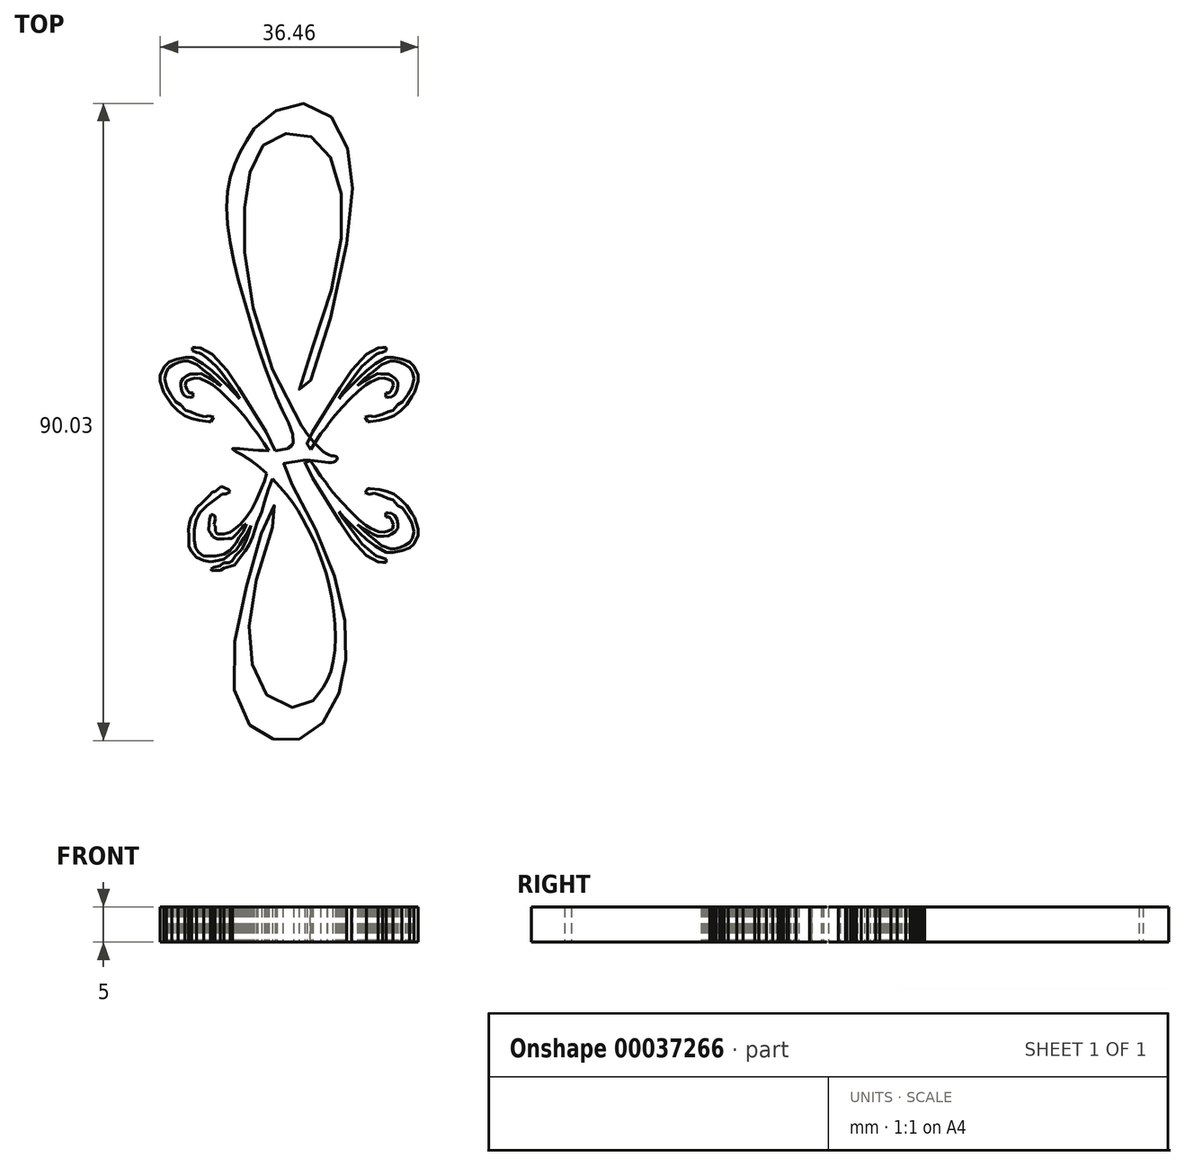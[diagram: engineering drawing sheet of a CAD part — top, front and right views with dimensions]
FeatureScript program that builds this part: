
annotation { "Feature Type Name" : "Feature", "Feature Type Description" : "" }
export const myFeature = defineFeature(function(context is Context, id is Id, definition is map)
    precondition{}
    {
        {
            var Q0;
            Q0=qCreatedBy(makeId("Top.planeOp"),FACE);
            var sketch = newSketch(context, id + "F0", { "sketchPlane" : qUnion([Q0])});
            skFitSpline(sketch, "E0", {"points": [v(-4.98, 52.48) * mm, v(-8.77, 43.42) * mm, v(-5.8, 26.25) * mm, v(-0.94, 12.64) * mm, v(0, 7.4) * mm, v(-8, 7.3) * mm, v(-6.47, 6.29) * mm, v(-0.6, 1.07) * mm, v(2.95, -4.65) * mm, v(5.7, -12.25) * mm, v(6.06, -23.55) * mm, v(3.37, -28.3) * mm], "startDerivative": vector(-52, -82.41) * mm, "endDerivative": vector(-44.36, -53.84) * mm});
            skFitSpline(sketch, "E1", {"points": [v(3.37, -28.3) * mm, v(0.95, -29.26) * mm, v(-3.07, -27.64) * mm, v(-5.46, -21.7) * mm, v(-4.69, -11.43) * mm, v(-1.8, -0.83) * mm, v(-2.3, -0.83) * mm, v(-5.52, -10.23) * mm, v(-7.9, -25.88) * mm, v(-4.68, -32.69) * mm, v(-1.17, -33.88) * mm, v(2.55, -33.39) * mm, v(6.27, -28.97) * mm, v(7.96, -23) * mm, v(7.32, -14.02) * mm, v(2.27, -1.25) * mm, v(-0.89, 5.13) * mm, v(-0.46, 5.24) * mm, v(2.3, 5.67) * mm, v(6.42, 5.45) * mm, v(6.75, 6.1) * mm, v(5.51, 6.44) * mm, v(-1.92, 17.38) * mm, v(-6.32, 34.87) * mm, v(-6.05, 43.62) * mm, v(-4.64, 48.73) * mm, v(-2.14, 51.4) * mm, v(1.12, 51.83) * mm, v(3.95, 50.9) * mm, v(6.55, 46.66) * mm, v(7.48, 38.19) * mm, v(4.22, 24.27) * mm, v(1.45, 15.15) * mm, v(2.32, 15.69) * mm, v(8.13, 36.5) * mm, v(8.57, 48.24) * mm, v(6.07, 54) * mm, v(1.88, 56.06) * mm, v(-1.87, 55.03) * mm, v(-4.98, 52.48) * mm], "startDerivative": vector(-130.49, -80) * mm, "endDerivative": vector(-141.72, -134) * mm});
            skLineSegment(sketch, "E2", {"start": v(-2.02, 7) * mm, "end": v(-3.27, 9.64) * mm});
            skLineSegment(sketch, "E3", {"start": v(-3.27, 9.64) * mm, "end": v(-7.15, 15.86) * mm});
            skLineSegment(sketch, "E4", {"start": v(-7.15, 15.86) * mm, "end": v(-8.78, 18.34) * mm});
            skLineSegment(sketch, "E5", {"start": v(-8.78, 18.34) * mm, "end": v(-10.9, 20.62) * mm});
            skLineSegment(sketch, "E6", {"start": v(-10.9, 20.62) * mm, "end": v(-12.53, 21.5) * mm});
            skLineSegment(sketch, "E7", {"start": v(-12.53, 21.5) * mm, "end": v(-13.21, 21.57) * mm});
            skLineSegment(sketch, "E8", {"start": v(-13.21, 21.57) * mm, "end": v(-13.68, 21.57) * mm});
            skLineSegment(sketch, "E9", {"start": v(-13.68, 21.57) * mm, "end": v(-13.68, 21.12) * mm});
            skLineSegment(sketch, "E10", {"start": v(-13.68, 21.12) * mm, "end": v(-13.13, 20.91) * mm});
            skLineSegment(sketch, "E11", {"start": v(-13.13, 20.91) * mm, "end": v(-12.73, 20.8) * mm});
            skLineSegment(sketch, "E12", {"start": v(-12.73, 20.8) * mm, "end": v(-12.31, 20.64) * mm});
            skLineSegment(sketch, "E13", {"start": v(-12.31, 20.64) * mm, "end": v(-11.6, 20.07) * mm});
            skLineSegment(sketch, "E14", {"start": v(-11.6, 20.07) * mm, "end": v(-10.29, 18.92) * mm});
            skLineSegment(sketch, "E15", {"start": v(-10.29, 18.92) * mm, "end": v(-9.6, 18.08) * mm});
            skLineSegment(sketch, "E16", {"start": v(-9.6, 18.08) * mm, "end": v(-7.57, 15.33) * mm});
            skLineSegment(sketch, "E17", {"start": v(-7.57, 15.33) * mm, "end": v(-7.02, 14.38) * mm});
            skLineSegment(sketch, "E18", {"start": v(-7.02, 14.38) * mm, "end": v(-7.75, 15.19) * mm});
            skLineSegment(sketch, "E19", {"start": v(-7.75, 15.19) * mm, "end": v(-8.94, 16.4) * mm});
            skLineSegment(sketch, "E20", {"start": v(-8.94, 16.4) * mm, "end": v(-9.87, 17.33) * mm});
            skLineSegment(sketch, "E21", {"start": v(-9.87, 17.33) * mm, "end": v(-10.96, 18.37) * mm});
            skLineSegment(sketch, "E22", {"start": v(-10.96, 18.37) * mm, "end": v(-12.2, 19.27) * mm});
            skLineSegment(sketch, "E23", {"start": v(-12.2, 19.27) * mm, "end": v(-13.69, 20.18) * mm});
            skLineSegment(sketch, "E24", {"start": v(-13.69, 20.18) * mm, "end": v(-14.65, 20.18) * mm});
            skLineSegment(sketch, "E25", {"start": v(-14.65, 20.18) * mm, "end": v(-15.93, 19.93) * mm});
            skLineSegment(sketch, "E26", {"start": v(-15.93, 19.93) * mm, "end": v(-16.96, 19.55) * mm});
            skLineSegment(sketch, "E27", {"start": v(-16.96, 19.55) * mm, "end": v(-17.62, 18.92) * mm});
            skLineSegment(sketch, "E28", {"start": v(-17.62, 18.92) * mm, "end": v(-18.23, 17.73) * mm});
            skLineSegment(sketch, "E29", {"start": v(-18.23, 17.73) * mm, "end": v(-18.23, 16.85) * mm});
            skLineSegment(sketch, "E30", {"start": v(-18.23, 16.85) * mm, "end": v(-17.72, 15.2) * mm});
            skLineSegment(sketch, "E31", {"start": v(-17.72, 15.2) * mm, "end": v(-17.34, 14.65) * mm});
            skLineSegment(sketch, "E32", {"start": v(-17.34, 14.65) * mm, "end": v(-16.6, 13.55) * mm});
            skLineSegment(sketch, "E33", {"start": v(-16.6, 13.55) * mm, "end": v(-15.74, 12.65) * mm});
            skLineSegment(sketch, "E34", {"start": v(-15.74, 12.65) * mm, "end": v(-14.75, 11.92) * mm});
            skLineSegment(sketch, "E35", {"start": v(-14.75, 11.92) * mm, "end": v(-13.78, 11.54) * mm});
            skLineSegment(sketch, "E36", {"start": v(-13.78, 11.54) * mm, "end": v(-12.74, 11.27) * mm});
            skLineSegment(sketch, "E37", {"start": v(-12.74, 11.27) * mm, "end": v(-11.4, 11.13) * mm});
            skLineSegment(sketch, "E38", {"start": v(-11.4, 11.13) * mm, "end": v(-11.1, 11.13) * mm});
            skLineSegment(sketch, "E39", {"start": v(-11.1, 11.13) * mm, "end": v(-10.69, 11.72) * mm});
            skLineSegment(sketch, "E40", {"start": v(-10.69, 11.72) * mm, "end": v(-11.34, 11.93) * mm});
            skLineSegment(sketch, "E41", {"start": v(-11.34, 11.93) * mm, "end": v(-11.97, 11.79) * mm});
            skLineSegment(sketch, "E42", {"start": v(-11.97, 11.79) * mm, "end": v(-13.1, 12.13) * mm});
            skLineSegment(sketch, "E43", {"start": v(-13.1, 12.13) * mm, "end": v(-13.94, 12.52) * mm});
            skLineSegment(sketch, "E44", {"start": v(-13.94, 12.52) * mm, "end": v(-14.63, 12.7) * mm});
            skLineSegment(sketch, "E45", {"start": v(-14.63, 12.7) * mm, "end": v(-15.38, 13.52) * mm});
            skLineSegment(sketch, "E46", {"start": v(-15.38, 13.52) * mm, "end": v(-16, 13.89) * mm});
            skLineSegment(sketch, "E47", {"start": v(-16, 13.89) * mm, "end": v(-16.73, 14.92) * mm});
            skLineSegment(sketch, "E48", {"start": v(-16.73, 14.92) * mm, "end": v(-17.32, 15.96) * mm});
            skLineSegment(sketch, "E49", {"start": v(-17.32, 15.96) * mm, "end": v(-17.61, 17.2) * mm});
            skLineSegment(sketch, "E50", {"start": v(-17.61, 17.2) * mm, "end": v(-17.39, 18.18) * mm});
            skLineSegment(sketch, "E51", {"start": v(-17.39, 18.18) * mm, "end": v(-17.01, 18.74) * mm});
            skLineSegment(sketch, "E52", {"start": v(-17.01, 18.74) * mm, "end": v(-16.37, 19.15) * mm});
            skLineSegment(sketch, "E53", {"start": v(-16.37, 19.15) * mm, "end": v(-15.65, 19.46) * mm});
            skLineSegment(sketch, "E54", {"start": v(-15.65, 19.46) * mm, "end": v(-14.9, 19.65) * mm});
            skLineSegment(sketch, "E55", {"start": v(-14.9, 19.65) * mm, "end": v(-14.33, 19.65) * mm});
            skLineSegment(sketch, "E56", {"start": v(-14.33, 19.65) * mm, "end": v(-13.07, 19.2) * mm});
            skLineSegment(sketch, "E57", {"start": v(-13.07, 19.2) * mm, "end": v(-11.84, 18.16) * mm});
            skLineSegment(sketch, "E58", {"start": v(-11.84, 18.16) * mm, "end": v(-11.22, 17.7) * mm});
            skLineSegment(sketch, "E59", {"start": v(-11.22, 17.7) * mm, "end": v(-10.54, 17.07) * mm});
            skLineSegment(sketch, "E60", {"start": v(-10.54, 17.07) * mm, "end": v(-10.05, 16.63) * mm});
            skLineSegment(sketch, "E61", {"start": v(-10.05, 16.63) * mm, "end": v(-9.63, 16.2) * mm});
            skLineSegment(sketch, "E62", {"start": v(-9.63, 16.2) * mm, "end": v(-10.22, 16.58) * mm});
            skLineSegment(sketch, "E63", {"start": v(-10.22, 16.58) * mm, "end": v(-10.56, 16.83) * mm});
            skLineSegment(sketch, "E64", {"start": v(-10.56, 16.83) * mm, "end": v(-11.37, 17.3) * mm});
            skLineSegment(sketch, "E65", {"start": v(-11.37, 17.3) * mm, "end": v(-11.78, 17.53) * mm});
            skLineSegment(sketch, "E66", {"start": v(-11.78, 17.53) * mm, "end": v(-12.48, 17.88) * mm});
            skLineSegment(sketch, "E67", {"start": v(-12.48, 17.88) * mm, "end": v(-12.9, 17.84) * mm});
            skLineSegment(sketch, "E68", {"start": v(-12.9, 17.84) * mm, "end": v(-13.36, 17.87) * mm});
            skLineSegment(sketch, "E69", {"start": v(-13.36, 17.87) * mm, "end": v(-14, 17.81) * mm});
            skLineSegment(sketch, "E70", {"start": v(-14, 17.81) * mm, "end": v(-14.47, 17.56) * mm});
            skLineSegment(sketch, "E71", {"start": v(-14.47, 17.56) * mm, "end": v(-15, 17.2) * mm});
            skLineSegment(sketch, "E72", {"start": v(-15, 17.2) * mm, "end": v(-15.35, 16.72) * mm});
            skLineSegment(sketch, "E73", {"start": v(-15.35, 16.72) * mm, "end": v(-15.35, 16.18) * mm});
            skLineSegment(sketch, "E74", {"start": v(-15.35, 16.18) * mm, "end": v(-15.22, 15.48) * mm});
            skLineSegment(sketch, "E75", {"start": v(-15.22, 15.48) * mm, "end": v(-14.93, 14.95) * mm});
            skLineSegment(sketch, "E76", {"start": v(-14.93, 14.95) * mm, "end": v(-14.48, 14.6) * mm});
            skLineSegment(sketch, "E77", {"start": v(-14.48, 14.6) * mm, "end": v(-13.93, 14.54) * mm});
            skLineSegment(sketch, "E78", {"start": v(-13.93, 14.54) * mm, "end": v(-13.63, 14.57) * mm});
            skLineSegment(sketch, "E79", {"start": v(-13.63, 14.57) * mm, "end": v(-13.63, 15.16) * mm});
            skLineSegment(sketch, "E80", {"start": v(-13.63, 15.16) * mm, "end": v(-14.12, 15.17) * mm});
            skLineSegment(sketch, "E81", {"start": v(-14.12, 15.17) * mm, "end": v(-14.46, 15.6) * mm});
            skLineSegment(sketch, "E82", {"start": v(-14.46, 15.6) * mm, "end": v(-14.7, 16.22) * mm});
            skLineSegment(sketch, "E83", {"start": v(-14.7, 16.22) * mm, "end": v(-14.58, 16.85) * mm});
            skLineSegment(sketch, "E84", {"start": v(-14.58, 16.85) * mm, "end": v(-14.02, 17.1) * mm});
            skLineSegment(sketch, "E85", {"start": v(-14.02, 17.1) * mm, "end": v(-13.36, 17.27) * mm});
            skLineSegment(sketch, "E86", {"start": v(-13.36, 17.27) * mm, "end": v(-12.62, 17.2) * mm});
            skLineSegment(sketch, "E87", {"start": v(-12.62, 17.2) * mm, "end": v(-11.5, 16.7) * mm});
            skLineSegment(sketch, "E88", {"start": v(-11.5, 16.7) * mm, "end": v(-10.84, 16.32) * mm});
            skLineSegment(sketch, "E89", {"start": v(-10.84, 16.32) * mm, "end": v(-9.74, 15.45) * mm});
            skLineSegment(sketch, "E90", {"start": v(-9.74, 15.45) * mm, "end": v(-8.7, 14.39) * mm});
            skLineSegment(sketch, "E91", {"start": v(-8.7, 14.39) * mm, "end": v(-7.42, 13.06) * mm});
            skLineSegment(sketch, "E92", {"start": v(-7.42, 13.06) * mm, "end": v(-6.14, 11.64) * mm});
            skLineSegment(sketch, "E93", {"start": v(-6.14, 11.64) * mm, "end": v(-5.4, 10.6) * mm});
            skLineSegment(sketch, "E94", {"start": v(-5.4, 10.6) * mm, "end": v(-5.29, 10.43) * mm});
            skLineSegment(sketch, "E95", {"start": v(-5.29, 10.43) * mm, "end": v(-4.44, 9.38) * mm});
            skLineSegment(sketch, "E96", {"start": v(-4.44, 9.38) * mm, "end": v(-3.6, 8.08) * mm});
            skLineSegment(sketch, "E97", {"start": v(-3.6, 8.08) * mm, "end": v(-2.89, 6.99) * mm});
            skLineSegment(sketch, "E98", {"start": v(-3.23, 3.82) * mm, "end": v(-3.53, 2.65) * mm});
            skLineSegment(sketch, "E99", {"start": v(-3.53, 2.65) * mm, "end": v(-4.67, 0) * mm});
            skLineSegment(sketch, "E100", {"start": v(-4.67, 0) * mm, "end": v(-5.32, -1.28) * mm});
            skLineSegment(sketch, "E101", {"start": v(-5.32, -1.28) * mm, "end": v(-5.98, -2.28) * mm});
            skLineSegment(sketch, "E102", {"start": v(-5.98, -2.28) * mm, "end": v(-6.87, -3.36) * mm});
            skLineSegment(sketch, "E103", {"start": v(-6.87, -3.36) * mm, "end": v(-7.87, -4.23) * mm});
            skLineSegment(sketch, "E104", {"start": v(-7.87, -4.23) * mm, "end": v(-8.32, -4.54) * mm});
            skLineSegment(sketch, "E105", {"start": v(-8.32, -4.54) * mm, "end": v(-9.22, -4.74) * mm});
            skLineSegment(sketch, "E106", {"start": v(-9.22, -4.74) * mm, "end": v(-10.16, -4.74) * mm});
            skLineSegment(sketch, "E107", {"start": v(-10.16, -4.74) * mm, "end": v(-10.42, -4.36) * mm});
            skLineSegment(sketch, "E108", {"start": v(-10.42, -4.36) * mm, "end": v(-10.42, -3.71) * mm});
            skLineSegment(sketch, "E109", {"start": v(-10.42, -3.71) * mm, "end": v(-10.63, -3.43) * mm});
            skLineSegment(sketch, "E110", {"start": v(-10.63, -3.43) * mm, "end": v(-10.45, -2.6) * mm});
            skLineSegment(sketch, "E111", {"start": v(-10.45, -2.6) * mm, "end": v(-10.54, -2.17) * mm});
            skLineSegment(sketch, "E112", {"start": v(-10.54, -2.17) * mm, "end": v(-10.74, -2.06) * mm});
            skLineSegment(sketch, "E113", {"start": v(-10.74, -2.06) * mm, "end": v(-11.05, -2.06) * mm});
            skLineSegment(sketch, "E114", {"start": v(-11.05, -2.06) * mm, "end": v(-11.3, -2.67) * mm});
            skLineSegment(sketch, "E115", {"start": v(-11.3, -2.67) * mm, "end": v(-11.31, -3.32) * mm});
            skLineSegment(sketch, "E116", {"start": v(-11.31, -3.32) * mm, "end": v(-11.38, -4.27) * mm});
            skLineSegment(sketch, "E117", {"start": v(-11.38, -4.27) * mm, "end": v(-11.1, -4.7) * mm});
            skLineSegment(sketch, "E118", {"start": v(-11.1, -4.7) * mm, "end": v(-10.84, -5.13) * mm});
            skLineSegment(sketch, "E119", {"start": v(-10.84, -5.13) * mm, "end": v(-10.2, -5.45) * mm});
            skLineSegment(sketch, "E120", {"start": v(-10.2, -5.45) * mm, "end": v(-9.22, -5.45) * mm});
            skLineSegment(sketch, "E121", {"start": v(-9.22, -5.45) * mm, "end": v(-8.63, -5.4) * mm});
            skLineSegment(sketch, "E122", {"start": v(-8.63, -5.4) * mm, "end": v(-8.1, -5.4) * mm});
            skLineSegment(sketch, "E123", {"start": v(-8.1, -5.4) * mm, "end": v(-7.24, -4.56) * mm});
            skLineSegment(sketch, "E124", {"start": v(-7.24, -4.56) * mm, "end": v(-6.54, -3.72) * mm});
            skLineSegment(sketch, "E125", {"start": v(-6.54, -3.72) * mm, "end": v(-6.03, -3.34) * mm});
            skLineSegment(sketch, "E126", {"start": v(-6.03, -3.34) * mm, "end": v(-6.5, -4.46) * mm});
            skLineSegment(sketch, "E127", {"start": v(-6.5, -4.46) * mm, "end": v(-7.07, -5.24) * mm});
            skLineSegment(sketch, "E128", {"start": v(-7.07, -5.24) * mm, "end": v(-7.52, -6.04) * mm});
            skLineSegment(sketch, "E129", {"start": v(-7.52, -6.04) * mm, "end": v(-8.32, -7.05) * mm});
            skLineSegment(sketch, "E130", {"start": v(-8.32, -7.05) * mm, "end": v(-9.24, -7.65) * mm});
            skLineSegment(sketch, "E131", {"start": v(-9.24, -7.65) * mm, "end": v(-10.41, -7.9) * mm});
            skLineSegment(sketch, "E132", {"start": v(-10.41, -7.9) * mm, "end": v(-11.4, -7.9) * mm});
            skLineSegment(sketch, "E133", {"start": v(-11.4, -7.9) * mm, "end": v(-12.18, -7.9) * mm});
            skLineSegment(sketch, "E134", {"start": v(-12.18, -7.9) * mm, "end": v(-12.86, -7.3) * mm});
            skLineSegment(sketch, "E135", {"start": v(-12.86, -7.3) * mm, "end": v(-13.25, -6.73) * mm});
            skLineSegment(sketch, "E136", {"start": v(-13.25, -6.73) * mm, "end": v(-13.4, -5.68) * mm});
            skLineSegment(sketch, "E137", {"start": v(-13.4, -5.68) * mm, "end": v(-13.43, -4.14) * mm});
            skLineSegment(sketch, "E138", {"start": v(-13.43, -4.14) * mm, "end": v(-13.19, -2.86) * mm});
            skLineSegment(sketch, "E139", {"start": v(-13.19, -2.86) * mm, "end": v(-12.68, -1.8) * mm});
            skLineSegment(sketch, "E140", {"start": v(-12.68, -1.8) * mm, "end": v(-11.68, -0.78) * mm});
            skLineSegment(sketch, "E141", {"start": v(-11.68, -0.78) * mm, "end": v(-10.65, 0) * mm});
            skLineSegment(sketch, "E142", {"start": v(-10.65, 0) * mm, "end": v(-9.85, 0.55) * mm});
            skLineSegment(sketch, "E143", {"start": v(-9.85, 0.55) * mm, "end": v(-9.48, 0.86) * mm});
            skLineSegment(sketch, "E144", {"start": v(-9.48, 0.86) * mm, "end": v(-8.95, 0.86) * mm});
            skLineSegment(sketch, "E145", {"start": v(-8.95, 0.86) * mm, "end": v(-8.37, 1.21) * mm});
            skLineSegment(sketch, "E146", {"start": v(-8.37, 1.21) * mm, "end": v(-8.58, 1.52) * mm});
            skLineSegment(sketch, "E147", {"start": v(-8.58, 1.52) * mm, "end": v(-9.6, 1.97) * mm});
            skLineSegment(sketch, "E148", {"start": v(-9.6, 1.97) * mm, "end": v(-10.5, 1.2) * mm});
            skLineSegment(sketch, "E149", {"start": v(-10.5, 1.2) * mm, "end": v(-10.84, 1.2) * mm});
            skLineSegment(sketch, "E150", {"start": v(-10.84, 1.2) * mm, "end": v(-11.37, 0.56) * mm});
            skLineSegment(sketch, "E151", {"start": v(-11.37, 0.56) * mm, "end": v(-12.27, -0.35) * mm});
            skLineSegment(sketch, "E152", {"start": v(-12.27, -0.35) * mm, "end": v(-13.01, -1.03) * mm});
            skLineSegment(sketch, "E153", {"start": v(-13.01, -1.03) * mm, "end": v(-13.62, -2.1) * mm});
            skLineSegment(sketch, "E154", {"start": v(-13.62, -2.1) * mm, "end": v(-13.85, -2.41) * mm});
            skLineSegment(sketch, "E155", {"start": v(-13.85, -2.41) * mm, "end": v(-14.03, -3.05) * mm});
            skLineSegment(sketch, "E156", {"start": v(-14.03, -3.05) * mm, "end": v(-14.23, -4.16) * mm});
            skLineSegment(sketch, "E157", {"start": v(-14.23, -4.16) * mm, "end": v(-14.2, -5.04) * mm});
            skLineSegment(sketch, "E158", {"start": v(-14.2, -5.04) * mm, "end": v(-14.2, -6.57) * mm});
            skLineSegment(sketch, "E159", {"start": v(-14.2, -6.57) * mm, "end": v(-13.8, -7.26) * mm});
            skLineSegment(sketch, "E160", {"start": v(-13.8, -7.26) * mm, "end": v(-13.1, -8.04) * mm});
            skLineSegment(sketch, "E161", {"start": v(-13.1, -8.04) * mm, "end": v(-12.11, -8.5) * mm});
            skLineSegment(sketch, "E162", {"start": v(-12.11, -8.5) * mm, "end": v(-11.1, -8.71) * mm});
            skLineSegment(sketch, "E163", {"start": v(-11.1, -8.71) * mm, "end": v(-10.08, -8.52) * mm});
            skLineSegment(sketch, "E164", {"start": v(-10.08, -8.52) * mm, "end": v(-9.26, -8.33) * mm});
            skLineSegment(sketch, "E165", {"start": v(-9.26, -8.33) * mm, "end": v(-8.46, -7.7) * mm});
            skLineSegment(sketch, "E166", {"start": v(-8.46, -7.7) * mm, "end": v(-7.54, -7.03) * mm});
            skLineSegment(sketch, "E167", {"start": v(-7.54, -7.03) * mm, "end": v(-7, -6.3) * mm});
            skLineSegment(sketch, "E168", {"start": v(-7, -6.3) * mm, "end": v(-6.41, -5.36) * mm});
            skLineSegment(sketch, "E169", {"start": v(-6.41, -5.36) * mm, "end": v(-5.9, -4.6) * mm});
            skLineSegment(sketch, "E170", {"start": v(-5.9, -4.6) * mm, "end": v(-5.43, -3.59) * mm});
            skLineSegment(sketch, "E171", {"start": v(-5.43, -3.59) * mm, "end": v(-5.76, -4.64) * mm});
            skLineSegment(sketch, "E172", {"start": v(-5.76, -4.64) * mm, "end": v(-6.14, -5.8) * mm});
            skLineSegment(sketch, "E173", {"start": v(-6.14, -5.8) * mm, "end": v(-6.77, -6.99) * mm});
            skLineSegment(sketch, "E174", {"start": v(-6.77, -6.99) * mm, "end": v(-7.57, -7.8) * mm});
            skLineSegment(sketch, "E175", {"start": v(-7.57, -7.8) * mm, "end": v(-8.08, -8.55) * mm});
            skLineSegment(sketch, "E176", {"start": v(-8.08, -8.55) * mm, "end": v(-8.56, -8.84) * mm});
            skLineSegment(sketch, "E177", {"start": v(-8.56, -8.84) * mm, "end": v(-9.27, -8.85) * mm});
            skLineSegment(sketch, "E178", {"start": v(-9.27, -8.85) * mm, "end": v(-9.78, -9.25) * mm});
            skLineSegment(sketch, "E179", {"start": v(-9.78, -9.25) * mm, "end": v(-10.6, -9.5) * mm});
            skLineSegment(sketch, "E180", {"start": v(-10.6, -9.5) * mm, "end": v(-11.1, -9.74) * mm});
            skLineSegment(sketch, "E181", {"start": v(-11.1, -9.74) * mm, "end": v(-10.96, -10) * mm});
            skLineSegment(sketch, "E182", {"start": v(-10.96, -10) * mm, "end": v(-10.5, -9.91) * mm});
            skLineSegment(sketch, "E183", {"start": v(-10.5, -9.91) * mm, "end": v(-9.74, -9.91) * mm});
            skLineSegment(sketch, "E184", {"start": v(-9.74, -9.91) * mm, "end": v(-9.23, -9.6) * mm});
            skLineSegment(sketch, "E185", {"start": v(-9.23, -9.6) * mm, "end": v(-8.32, -9.37) * mm});
            skLineSegment(sketch, "E186", {"start": v(-8.32, -9.37) * mm, "end": v(-7.69, -9.14) * mm});
            skLineSegment(sketch, "E187", {"start": v(-7.69, -9.14) * mm, "end": v(-6.89, -8.03) * mm});
            skLineSegment(sketch, "E188", {"start": v(-6.89, -8.03) * mm, "end": v(-6.24, -7.18) * mm});
            skLineSegment(sketch, "E189", {"start": v(-6.24, -7.18) * mm, "end": v(-5.7, -6.27) * mm});
            skLineSegment(sketch, "E190", {"start": v(-5.7, -6.27) * mm, "end": v(-5.2, -5.16) * mm});
            skLineSegment(sketch, "E191", {"start": v(-5.2, -5.16) * mm, "end": v(-4.53, -3.14) * mm});
            skLineSegment(sketch, "E192", {"start": v(-4.53, -3.14) * mm, "end": v(-3.9, -1.64) * mm});
            skLineSegment(sketch, "E193", {"start": v(-3.9, -1.64) * mm, "end": v(-3.49, -0.28) * mm});
            skLineSegment(sketch, "E194", {"start": v(-3.49, -0.28) * mm, "end": v(-2.97, 1.56) * mm});
            skLineSegment(sketch, "E195", {"start": v(-2.97, 1.56) * mm, "end": v(-2.4, 3.03) * mm});
            skLineSegment(sketch, "E196", {"start": v(1.96, 5.66) * mm, "end": v(1.96, 4.6) * mm});
            skLineSegment(sketch, "E197", {"start": v(1.96, 4.6) * mm, "end": v(2.18, 3.77) * mm});
            skLineSegment(sketch, "E198", {"start": v(2.18, 3.77) * mm, "end": v(2.43, 2.6) * mm});
            skLineSegment(sketch, "E199", {"start": v(2.43, 2.6) * mm, "end": v(2.7, 1.46) * mm});
            skLineSegment(sketch, "E200", {"start": v(2.7, 1.46) * mm, "end": v(2.95, 0.59) * mm});
            skLineSegment(sketch, "E201", {"start": v(2.95, 0.59) * mm, "end": v(3.28, -0.15) * mm});
            skLineSegment(sketch, "E202", {"start": v(3.28, -0.15) * mm, "end": v(3.44, -1.19) * mm});
            skLineSegment(sketch, "E203", {"start": v(3.44, -1.19) * mm, "end": v(4.07, -2.5) * mm});
            skLineSegment(sketch, "E204", {"start": v(4.07, -2.5) * mm, "end": v(4.28, -3.22) * mm});
            skLineSegment(sketch, "E205", {"start": v(4.28, -3.22) * mm, "end": v(4.63, -3.77) * mm});
            skLineSegment(sketch, "E206", {"start": v(4.63, -3.77) * mm, "end": v(5.03, -4.34) * mm});
            skLineSegment(sketch, "E207", {"start": v(5.03, -4.34) * mm, "end": v(5.42, -4.97) * mm});
            skLineSegment(sketch, "E208", {"start": v(5.42, -4.97) * mm, "end": v(5.9, -5.47) * mm});
            skLineSegment(sketch, "E209", {"start": v(5.9, -5.47) * mm, "end": v(6.98, -6.44) * mm});
            skLineSegment(sketch, "E210", {"start": v(6.98, -6.44) * mm, "end": v(7.3, -6.55) * mm});
            skLineSegment(sketch, "E211", {"start": v(7.3, -6.55) * mm, "end": v(7.53, -6.73) * mm});
            skLineSegment(sketch, "E212", {"start": v(7.53, -6.73) * mm, "end": v(7.85, -6.8) * mm});
            skLineSegment(sketch, "E213", {"start": v(7.85, -6.8) * mm, "end": v(8.32, -6.66) * mm});
            skLineSegment(sketch, "E214", {"start": v(8.32, -6.66) * mm, "end": v(7.94, -6.02) * mm});
            skLineSegment(sketch, "E215", {"start": v(7.94, -6.02) * mm, "end": v(7.48, -5.93) * mm});
            skLineSegment(sketch, "E216", {"start": v(7.48, -5.93) * mm, "end": v(7.04, -5.33) * mm});
            skLineSegment(sketch, "E217", {"start": v(7.04, -5.33) * mm, "end": v(6.23, -4.45) * mm});
            skLineSegment(sketch, "E218", {"start": v(6.23, -4.45) * mm, "end": v(5.6, -3.74) * mm});
            skLineSegment(sketch, "E219", {"start": v(5.6, -3.74) * mm, "end": v(5.25, -3) * mm});
            skLineSegment(sketch, "E220", {"start": v(5.25, -3) * mm, "end": v(4.83, -2.43) * mm});
            skLineSegment(sketch, "E221", {"start": v(4.83, -2.43) * mm, "end": v(4.37, -1.28) * mm});
            skLineSegment(sketch, "E222", {"start": v(4.37, -1.28) * mm, "end": v(4.02, -0.15) * mm});
            skLineSegment(sketch, "E223", {"start": v(4.02, -0.15) * mm, "end": v(3.88, 0.34) * mm});
            skLineSegment(sketch, "E224", {"start": v(3.88, 0.34) * mm, "end": v(3.5, 1.44) * mm});
            skLineSegment(sketch, "E225", {"start": v(3.5, 1.44) * mm, "end": v(3.31, 1.86) * mm});
            skLineSegment(sketch, "E226", {"start": v(3.31, 1.86) * mm, "end": v(3.31, 2.34) * mm});
            skLineSegment(sketch, "E227", {"start": v(3.31, 2.34) * mm, "end": v(3.82, 1.58) * mm});
            skLineSegment(sketch, "E228", {"start": v(3.82, 1.58) * mm, "end": v(4.08, 0.94) * mm});
            skLineSegment(sketch, "E229", {"start": v(4.08, 0.94) * mm, "end": v(4.68, 0) * mm});
            skLineSegment(sketch, "E230", {"start": v(4.68, 0) * mm, "end": v(5.34, -1.11) * mm});
            skLineSegment(sketch, "E231", {"start": v(5.34, -1.11) * mm, "end": v(5.76, -2.03) * mm});
            skLineSegment(sketch, "E232", {"start": v(5.76, -2.03) * mm, "end": v(6.36, -2.65) * mm});
            skLineSegment(sketch, "E233", {"start": v(6.36, -2.65) * mm, "end": v(7.17, -3.8) * mm});
            skLineSegment(sketch, "E234", {"start": v(7.17, -3.8) * mm, "end": v(8.12, -4.56) * mm});
            skLineSegment(sketch, "E235", {"start": v(8.12, -4.56) * mm, "end": v(9.14, -5.04) * mm});
            skLineSegment(sketch, "E236", {"start": v(9.14, -5.04) * mm, "end": v(10.09, -5.36) * mm});
            skLineSegment(sketch, "E237", {"start": v(10.09, -5.36) * mm, "end": v(10.57, -5.38) * mm});
            skLineSegment(sketch, "E238", {"start": v(10.57, -5.38) * mm, "end": v(11.58, -4.87) * mm});
            skLineSegment(sketch, "E239", {"start": v(11.58, -4.87) * mm, "end": v(12.69, -4.15) * mm});
            skLineSegment(sketch, "E240", {"start": v(12.69, -4.15) * mm, "end": v(13.54, -2.83) * mm});
            skLineSegment(sketch, "E241", {"start": v(13.54, -2.83) * mm, "end": v(13.51, -2.18) * mm});
            skLineSegment(sketch, "E242", {"start": v(13.51, -2.18) * mm, "end": v(13.46, -1.47) * mm});
            skLineSegment(sketch, "E243", {"start": v(13.46, -1.47) * mm, "end": v(13.18, -0.94) * mm});
            skLineSegment(sketch, "E244", {"start": v(13.18, -0.94) * mm, "end": v(12.72, 0.03) * mm});
            skLineSegment(sketch, "E245", {"start": v(12.72, 0.03) * mm, "end": v(11.9, 1.18) * mm});
            skLineSegment(sketch, "E246", {"start": v(11.9, 1.18) * mm, "end": v(11.1, 2.03) * mm});
            skLineSegment(sketch, "E247", {"start": v(11.1, 2.03) * mm, "end": v(11.02, 2.28) * mm});
            skLineSegment(sketch, "E248", {"start": v(11.02, 2.28) * mm, "end": v(10.4, 2.67) * mm});
            skLineSegment(sketch, "E249", {"start": v(10.4, 2.67) * mm, "end": v(9.47, 2.67) * mm});
            skLineSegment(sketch, "E250", {"start": v(9.47, 2.67) * mm, "end": v(8.74, 2.6) * mm});
            skLineSegment(sketch, "E251", {"start": v(8.74, 2.6) * mm, "end": v(8.4, 2.37) * mm});
            skLineSegment(sketch, "E252", {"start": v(8.4, 2.37) * mm, "end": v(8.12, 2) * mm});
            skLineSegment(sketch, "E253", {"start": v(8.12, 2) * mm, "end": v(8.07, 1.76) * mm});
            skLineSegment(sketch, "E254", {"start": v(8.07, 1.76) * mm, "end": v(8.3, 1.63) * mm});
            skLineSegment(sketch, "E255", {"start": v(8.3, 1.63) * mm, "end": v(8.76, 1.65) * mm});
            skLineSegment(sketch, "E256", {"start": v(8.76, 1.65) * mm, "end": v(9.13, 1.98) * mm});
            skLineSegment(sketch, "E257", {"start": v(9.13, 1.98) * mm, "end": v(9.85, 2.07) * mm});
            skLineSegment(sketch, "E258", {"start": v(9.85, 2.07) * mm, "end": v(10.38, 1.82) * mm});
            skLineSegment(sketch, "E259", {"start": v(10.38, 1.82) * mm, "end": v(10.82, 1.13) * mm});
            skLineSegment(sketch, "E260", {"start": v(10.82, 1.13) * mm, "end": v(11.45, 0.37) * mm});
            skLineSegment(sketch, "E261", {"start": v(11.45, 0.37) * mm, "end": v(12.07, -0.48) * mm});
            skLineSegment(sketch, "E262", {"start": v(12.07, -0.48) * mm, "end": v(12.56, -1.45) * mm});
            skLineSegment(sketch, "E263", {"start": v(12.56, -1.45) * mm, "end": v(12.77, -2.35) * mm});
            skLineSegment(sketch, "E264", {"start": v(12.77, -2.35) * mm, "end": v(12.3, -3.2) * mm});
            skLineSegment(sketch, "E265", {"start": v(12.3, -3.2) * mm, "end": v(11.6, -3.92) * mm});
            skLineSegment(sketch, "E266", {"start": v(11.6, -3.92) * mm, "end": v(10.8, -4.48) * mm});
            skLineSegment(sketch, "E267", {"start": v(10.8, -4.48) * mm, "end": v(9.57, -4.32) * mm});
            skLineSegment(sketch, "E268", {"start": v(9.57, -4.32) * mm, "end": v(8.37, -3.78) * mm});
            skLineSegment(sketch, "E269", {"start": v(8.37, -3.78) * mm, "end": v(7.9, -3.48) * mm});
            skLineSegment(sketch, "E270", {"start": v(7.9, -3.48) * mm, "end": v(7.35, -2.63) * mm});
            skLineSegment(sketch, "E271", {"start": v(7.35, -2.63) * mm, "end": v(6.35, -1.57) * mm});
            skLineSegment(sketch, "E272", {"start": v(6.35, -1.57) * mm, "end": v(5.93, -0.58) * mm});
            skLineSegment(sketch, "E273", {"start": v(5.93, -0.58) * mm, "end": v(6.68, -1.43) * mm});
            skLineSegment(sketch, "E274", {"start": v(6.68, -1.43) * mm, "end": v(7.95, -2.37) * mm});
            skLineSegment(sketch, "E275", {"start": v(7.95, -2.37) * mm, "end": v(8.3, -2.37) * mm});
            skLineSegment(sketch, "E276", {"start": v(8.3, -2.37) * mm, "end": v(8.53, -2.69) * mm});
            skLineSegment(sketch, "E277", {"start": v(8.53, -2.69) * mm, "end": v(9.57, -2.68) * mm});
            skLineSegment(sketch, "E278", {"start": v(9.57, -2.68) * mm, "end": v(10.47, -2.82) * mm});
            skLineSegment(sketch, "E279", {"start": v(10.47, -2.82) * mm, "end": v(11.39, -2.5) * mm});
            skLineSegment(sketch, "E280", {"start": v(11.39, -2.5) * mm, "end": v(11.94, -1.87) * mm});
            skLineSegment(sketch, "E281", {"start": v(11.94, -1.87) * mm, "end": v(11.75, -0.94) * mm});
            skLineSegment(sketch, "E282", {"start": v(11.75, -0.94) * mm, "end": v(11.5, -0.58) * mm});
            skLineSegment(sketch, "E283", {"start": v(11.5, -0.58) * mm, "end": v(10.94, -0.58) * mm});
            skLineSegment(sketch, "E284", {"start": v(10.94, -0.58) * mm, "end": v(10.7, -1) * mm});
            skLineSegment(sketch, "E285", {"start": v(10.7, -1) * mm, "end": v(11.04, -1.2) * mm});
            skLineSegment(sketch, "E286", {"start": v(11.04, -1.2) * mm, "end": v(11.13, -1.5) * mm});
            skLineSegment(sketch, "E287", {"start": v(11.13, -1.5) * mm, "end": v(10.79, -1.9) * mm});
            skLineSegment(sketch, "E288", {"start": v(10.79, -1.9) * mm, "end": v(9.98, -1.9) * mm});
            skLineSegment(sketch, "E289", {"start": v(9.98, -1.9) * mm, "end": v(9.03, -1.76) * mm});
            skLineSegment(sketch, "E290", {"start": v(9.03, -1.76) * mm, "end": v(8.48, -1.76) * mm});
            skLineSegment(sketch, "E291", {"start": v(8.48, -1.76) * mm, "end": v(8.08, -1.47) * mm});
            skLineSegment(sketch, "E292", {"start": v(8.08, -1.47) * mm, "end": v(7.58, -1.08) * mm});
            skLineSegment(sketch, "E293", {"start": v(7.58, -1.08) * mm, "end": v(7.09, -0.62) * mm});
            skLineSegment(sketch, "E294", {"start": v(7.09, -0.62) * mm, "end": v(6.25, 0.2) * mm});
            skLineSegment(sketch, "E295", {"start": v(6.25, 0.2) * mm, "end": v(5.67, 1.15) * mm});
            skLineSegment(sketch, "E296", {"start": v(5.67, 1.15) * mm, "end": v(4.51, 2.56) * mm});
            skLineSegment(sketch, "E297", {"start": v(4.51, 2.56) * mm, "end": v(3.77, 3.48) * mm});
            skLineSegment(sketch, "E298", {"start": v(3.77, 3.48) * mm, "end": v(3.21, 4.49) * mm});
            skLineSegment(sketch, "E299", {"start": v(3.21, 4.49) * mm, "end": v(2.98, 5.11) * mm});
            skLineSegment(sketch, "E300", {"start": v(2.98, 5.11) * mm, "end": v(2.97, 5.67) * mm});
            skLineSegment(sketch, "E301", {"start": v(1.78, 10.48) * mm, "end": v(2.2, 12.94) * mm});
            skLineSegment(sketch, "E302", {"start": v(2.2, 12.94) * mm, "end": v(2.95, 15.5) * mm});
            skLineSegment(sketch, "E303", {"start": v(2.95, 15.5) * mm, "end": v(3.52, 17.36) * mm});
            skLineSegment(sketch, "E304", {"start": v(3.52, 17.36) * mm, "end": v(4.36, 19.75) * mm});
            skLineSegment(sketch, "E305", {"start": v(4.36, 19.75) * mm, "end": v(5.04, 21.57) * mm});
            skLineSegment(sketch, "E306", {"start": v(5.04, 21.57) * mm, "end": v(5.76, 22.66) * mm});
            skLineSegment(sketch, "E307", {"start": v(5.76, 22.66) * mm, "end": v(6.88, 24.04) * mm});
            skLineSegment(sketch, "E308", {"start": v(6.88, 24.04) * mm, "end": v(7.96, 25.1) * mm});
            skLineSegment(sketch, "E309", {"start": v(7.96, 25.1) * mm, "end": v(8.83, 25.75) * mm});
            skLineSegment(sketch, "E310", {"start": v(8.83, 25.75) * mm, "end": v(9.25, 26.14) * mm});
            skLineSegment(sketch, "E311", {"start": v(9.25, 26.14) * mm, "end": v(9.76, 26.14) * mm});
            skLineSegment(sketch, "E312", {"start": v(9.76, 26.14) * mm, "end": v(9.93, 25.83) * mm});
            skLineSegment(sketch, "E313", {"start": v(9.93, 25.83) * mm, "end": v(9.7, 25.24) * mm});
            skLineSegment(sketch, "E314", {"start": v(9.7, 25.24) * mm, "end": v(9.2, 24.73) * mm});
            skLineSegment(sketch, "E315", {"start": v(9.2, 24.73) * mm, "end": v(8.63, 24.14) * mm});
            skLineSegment(sketch, "E316", {"start": v(8.63, 24.14) * mm, "end": v(7.5, 23.38) * mm});
            skLineSegment(sketch, "E317", {"start": v(7.5, 23.38) * mm, "end": v(6.94, 22.79) * mm});
            skLineSegment(sketch, "E318", {"start": v(6.94, 22.79) * mm, "end": v(6.43, 22.17) * mm});
            skLineSegment(sketch, "E319", {"start": v(6.43, 22.17) * mm, "end": v(5.9, 21.3) * mm});
            skLineSegment(sketch, "E320", {"start": v(5.9, 21.3) * mm, "end": v(5.28, 20.06) * mm});
            skLineSegment(sketch, "E321", {"start": v(5.28, 20.06) * mm, "end": v(4.9, 19.27) * mm});
            skLineSegment(sketch, "E322", {"start": v(4.9, 19.27) * mm, "end": v(4.51, 18.25) * mm});
            skLineSegment(sketch, "E323", {"start": v(4.51, 18.25) * mm, "end": v(5.36, 19.4) * mm});
            skLineSegment(sketch, "E324", {"start": v(5.36, 19.4) * mm, "end": v(5.7, 20.17) * mm});
            skLineSegment(sketch, "E325", {"start": v(5.7, 20.17) * mm, "end": v(6.29, 21.18) * mm});
            skLineSegment(sketch, "E326", {"start": v(6.29, 21.18) * mm, "end": v(7.22, 22.34) * mm});
            skLineSegment(sketch, "E327", {"start": v(7.22, 22.34) * mm, "end": v(7.98, 23.16) * mm});
            skLineSegment(sketch, "E328", {"start": v(7.98, 23.16) * mm, "end": v(8.97, 23.64) * mm});
            skLineSegment(sketch, "E329", {"start": v(8.97, 23.64) * mm, "end": v(10.24, 23.97) * mm});
            skLineSegment(sketch, "E330", {"start": v(10.24, 23.97) * mm, "end": v(11.28, 23.72) * mm});
            skLineSegment(sketch, "E331", {"start": v(11.28, 23.72) * mm, "end": v(12.26, 23.27) * mm});
            skLineSegment(sketch, "E332", {"start": v(12.26, 23.27) * mm, "end": v(12.94, 22.93) * mm});
            skLineSegment(sketch, "E333", {"start": v(12.94, 22.93) * mm, "end": v(13.79, 22.03) * mm});
            skLineSegment(sketch, "E334", {"start": v(13.79, 22.03) * mm, "end": v(14.2, 20.99) * mm});
            skLineSegment(sketch, "E335", {"start": v(14.2, 20.99) * mm, "end": v(14.32, 19.8) * mm});
            skLineSegment(sketch, "E336", {"start": v(14.32, 19.8) * mm, "end": v(14.27, 18.96) * mm});
            skLineSegment(sketch, "E337", {"start": v(14.27, 18.96) * mm, "end": v(13.84, 17.43) * mm});
            skLineSegment(sketch, "E338", {"start": v(13.84, 17.43) * mm, "end": v(13.34, 16.22) * mm});
            skLineSegment(sketch, "E339", {"start": v(13.34, 16.22) * mm, "end": v(12.49, 14.64) * mm});
            skLineSegment(sketch, "E340", {"start": v(12.49, 14.64) * mm, "end": v(11.59, 13.66) * mm});
            skLineSegment(sketch, "E341", {"start": v(11.59, 13.66) * mm, "end": v(10.74, 12.78) * mm});
            skLineSegment(sketch, "E342", {"start": v(10.74, 12.78) * mm, "end": v(9.73, 12.16) * mm});
            skLineSegment(sketch, "E343", {"start": v(9.73, 12.16) * mm, "end": v(8.94, 12.28) * mm});
            skLineSegment(sketch, "E344", {"start": v(8.94, 12.28) * mm, "end": v(8.12, 12.3) * mm});
            skLineSegment(sketch, "E345", {"start": v(8.12, 12.3) * mm, "end": v(7.16, 12.73) * mm});
            skLineSegment(sketch, "E346", {"start": v(7.16, 12.73) * mm, "end": v(6.9, 13.04) * mm});
            skLineSegment(sketch, "E347", {"start": v(6.9, 13.04) * mm, "end": v(6.63, 13.94) * mm});
            skLineSegment(sketch, "E348", {"start": v(6.63, 13.94) * mm, "end": v(6.88, 14.28) * mm});
            skLineSegment(sketch, "E349", {"start": v(6.88, 14.28) * mm, "end": v(7.14, 14.1) * mm});
            skLineSegment(sketch, "E350", {"start": v(7.14, 14.1) * mm, "end": v(7.45, 14) * mm});
            skLineSegment(sketch, "E351", {"start": v(7.45, 14) * mm, "end": v(7.45, 13.57) * mm});
            skLineSegment(sketch, "E352", {"start": v(7.45, 13.57) * mm, "end": v(7.53, 13.32) * mm});
            skLineSegment(sketch, "E353", {"start": v(7.53, 13.32) * mm, "end": v(7.92, 13.12) * mm});
            skLineSegment(sketch, "E354", {"start": v(7.92, 13.12) * mm, "end": v(8.3, 13.04) * mm});
            skLineSegment(sketch, "E355", {"start": v(8.3, 13.04) * mm, "end": v(8.66, 12.87) * mm});
            skLineSegment(sketch, "E356", {"start": v(8.66, 12.87) * mm, "end": v(9.22, 12.98) * mm});
            skLineSegment(sketch, "E357", {"start": v(9.22, 12.98) * mm, "end": v(9.62, 13.18) * mm});
            skLineSegment(sketch, "E358", {"start": v(9.62, 13.18) * mm, "end": v(11.08, 14.2) * mm});
            skLineSegment(sketch, "E359", {"start": v(11.08, 14.2) * mm, "end": v(11.53, 14.7) * mm});
            skLineSegment(sketch, "E360", {"start": v(11.53, 14.7) * mm, "end": v(11.87, 15.18) * mm});
            skLineSegment(sketch, "E361", {"start": v(11.87, 15.18) * mm, "end": v(12.2, 15.91) * mm});
            skLineSegment(sketch, "E362", {"start": v(12.2, 15.91) * mm, "end": v(12.77, 17.1) * mm});
            skLineSegment(sketch, "E363", {"start": v(12.77, 17.1) * mm, "end": v(13.05, 17.97) * mm});
            skLineSegment(sketch, "E364", {"start": v(13.05, 17.97) * mm, "end": v(13.36, 18.96) * mm});
            skLineSegment(sketch, "E365", {"start": v(13.36, 18.96) * mm, "end": v(13.4, 20.14) * mm});
            skLineSegment(sketch, "E366", {"start": v(13.4, 20.14) * mm, "end": v(13.1, 21.32) * mm});
            skLineSegment(sketch, "E367", {"start": v(13.1, 21.32) * mm, "end": v(12.8, 21.89) * mm});
            skLineSegment(sketch, "E368", {"start": v(12.8, 21.89) * mm, "end": v(12.07, 22.5) * mm});
            skLineSegment(sketch, "E369", {"start": v(12.07, 22.5) * mm, "end": v(11, 22.96) * mm});
            skLineSegment(sketch, "E370", {"start": v(11, 22.96) * mm, "end": v(10.4, 23.1) * mm});
            skLineSegment(sketch, "E371", {"start": v(10.4, 23.1) * mm, "end": v(9.39, 22.9) * mm});
            skLineSegment(sketch, "E372", {"start": v(9.39, 22.9) * mm, "end": v(8.4, 22.42) * mm});
            skLineSegment(sketch, "E373", {"start": v(8.4, 22.42) * mm, "end": v(7.84, 21.75) * mm});
            skLineSegment(sketch, "E374", {"start": v(7.84, 21.75) * mm, "end": v(7.5, 21.32) * mm});
            skLineSegment(sketch, "E375", {"start": v(7.5, 21.32) * mm, "end": v(8.35, 21.89) * mm});
            skLineSegment(sketch, "E376", {"start": v(8.35, 21.89) * mm, "end": v(9.16, 22.11) * mm});
            skLineSegment(sketch, "E377", {"start": v(9.16, 22.11) * mm, "end": v(10.1, 22.03) * mm});
            skLineSegment(sketch, "E378", {"start": v(10.1, 22.03) * mm, "end": v(10.86, 21.7) * mm});
            skLineSegment(sketch, "E379", {"start": v(10.86, 21.7) * mm, "end": v(11.64, 21.04) * mm});
            skLineSegment(sketch, "E380", {"start": v(11.64, 21.04) * mm, "end": v(12.1, 20.3) * mm});
            skLineSegment(sketch, "E381", {"start": v(12.1, 20.3) * mm, "end": v(12.25, 19) * mm});
            skLineSegment(sketch, "E382", {"start": v(12.25, 19) * mm, "end": v(12.2, 17.9) * mm});
            skLineSegment(sketch, "E383", {"start": v(12.2, 17.9) * mm, "end": v(11.78, 16.78) * mm});
            skLineSegment(sketch, "E384", {"start": v(11.78, 16.78) * mm, "end": v(11.38, 16.05) * mm});
            skLineSegment(sketch, "E385", {"start": v(11.38, 16.05) * mm, "end": v(10.82, 15.9) * mm});
            skLineSegment(sketch, "E386", {"start": v(10.82, 15.9) * mm, "end": v(10.55, 16.1) * mm});
            skLineSegment(sketch, "E387", {"start": v(10.55, 16.1) * mm, "end": v(10.64, 16.39) * mm});
            skLineSegment(sketch, "E388", {"start": v(10.64, 16.39) * mm, "end": v(11.12, 17.17) * mm});
            skLineSegment(sketch, "E389", {"start": v(11.12, 17.17) * mm, "end": v(11.4, 17.96) * mm});
            skLineSegment(sketch, "E390", {"start": v(11.4, 17.96) * mm, "end": v(11.5, 19.23) * mm});
            skLineSegment(sketch, "E391", {"start": v(11.5, 19.23) * mm, "end": v(11.17, 20.42) * mm});
            skLineSegment(sketch, "E392", {"start": v(11.17, 20.42) * mm, "end": v(10.38, 21.03) * mm});
            skLineSegment(sketch, "E393", {"start": v(10.38, 21.03) * mm, "end": v(9.7, 21.18) * mm});
            skLineSegment(sketch, "E394", {"start": v(9.7, 21.18) * mm, "end": v(9.02, 21.17) * mm});
            skLineSegment(sketch, "E395", {"start": v(9.02, 21.17) * mm, "end": v(8.14, 20.9) * mm});
            skLineSegment(sketch, "E396", {"start": v(8.14, 20.9) * mm, "end": v(7.43, 20.4) * mm});
            skLineSegment(sketch, "E397", {"start": v(7.43, 20.4) * mm, "end": v(6.85, 19.72) * mm});
            skLineSegment(sketch, "E398", {"start": v(6.85, 19.72) * mm, "end": v(6.33, 19.13) * mm});
            skLineSegment(sketch, "E399", {"start": v(6.33, 19.13) * mm, "end": v(5.85, 18.67) * mm});
            skLineSegment(sketch, "E400", {"start": v(5.85, 18.67) * mm, "end": v(5.32, 17.76) * mm});
            skLineSegment(sketch, "E401", {"start": v(5.32, 17.76) * mm, "end": v(4.84, 16.97) * mm});
            skLineSegment(sketch, "E402", {"start": v(4.84, 16.97) * mm, "end": v(4.3, 15.92) * mm});
            skLineSegment(sketch, "E403", {"start": v(4.3, 15.92) * mm, "end": v(3.87, 14.86) * mm});
            skLineSegment(sketch, "E404", {"start": v(3.87, 14.86) * mm, "end": v(3.38, 13.63) * mm});
            skLineSegment(sketch, "E405", {"start": v(3.38, 13.63) * mm, "end": v(2.97, 12.32) * mm});
            skLineSegment(sketch, "E406", {"start": v(2.97, 12.32) * mm, "end": v(2.76, 11.03) * mm});
            skLineSegment(sketch, "E407", {"start": v(2.76, 11.03) * mm, "end": v(2.65, 9.9) * mm});
            skLineSegment(sketch, "E408", {"start": v(2.65, 9.9) * mm, "end": v(2.51, 9.41) * mm});
            skLineSegment(sketch, "E409", {"start": v(0, 0) * mm, "end": v(0, 42.4) * mm, "construction": true});
            skLineSegment(sketch, "E410", {"start": v(0, 42.4) * mm, "end": v(0, -42.56) * mm, "construction": true});
            skSolve(sketch);
        }
        {
            var Q0;
            Q0=qCreatedBy(makeId("Top.planeOp"),FACE);
            var sketch = newSketch(context, id + "F1", { "sketchPlane" : qUnion([Q0])});
            skLineSegment(sketch, "E411.0", {"start": v(0, 42.4) * mm, "end": v(0, -42.56) * mm, "construction": true});
            skFitSpline(sketch, "E412.0.0", {"points": [v(3.37, -28.3) * mm, v(2.64, -28.75) * mm, v(0.97, -29.78) * mm, v(-3.9, -28.1) * mm, v(-5.97, -21.21) * mm, v(-5.66, -12.35) * mm, v(-0.94, -0.6) * mm, v(-2.98, -0.7) * mm, v(-5.8, -11.23) * mm, v(-9.45, -25.33) * mm, v(-5.3, -33.23) * mm, v(-1.2, -33.98) * mm, v(2.96, -34.06) * mm, v(6.73, -28.91) * mm, v(8.34, -22.9) * mm, v(7.92, -13.57) * mm, v(3.1, -2.23) * mm, v(-1.5, 5.38) * mm, v(-0.28, 5.14) * mm, v(2.25, 6.15) * mm, v(6.47, 4.82) * mm, v(6.99, 6.4) * mm, v(4.54, 5.76) * mm, v(-3.4, 17.92) * mm, v(-6.87, 34.35) * mm, v(-6.27, 43.3) * mm, v(-5.05, 48.74) * mm, v(-2.39, 51.82) * mm, v(1.15, 51.95) * mm, v(4.34, 51.28) * mm, v(7.11, 46.45) * mm, v(8.14, 37.68) * mm, v(4.93, 25.47) * mm, v(0.5, 14.37) * mm, v(3.53, 15.95) * mm, v(8.93, 37.32) * mm, v(9.2, 47.62) * mm, v(6.74, 54.38) * mm, v(1.93, 56.64) * mm, v(-2.04, 55.26) * mm, v(-4, 53.4) * mm, v(-4.98, 52.48) * mm]});
            skFitSpline(sketch, "E412.0.1", {"points": [v(-4.98, 52.48) * mm, v(-6.7, 49.75) * mm, v(-10.62, 43.5) * mm, v(-5.88, 25.99) * mm, v(-1.87, 13.77) * mm, v(2.92, 5.59) * mm, v(-10.1, 7.98) * mm, v(-5.6, 6.1) * mm, v(-0.18, 1.21) * mm, v(3.1, -4.7) * mm, v(6.22, -11.96) * mm, v(7.06, -23.76) * mm, v(4.47, -26.98) * mm, v(3.37, -28.3) * mm]});
            skFitSpline(sketch, "E412.0.2", {"points": [v(-4.98, 52.48) * mm, v(-6.7, 49.75) * mm, v(-10.62, 43.5) * mm, v(-5.88, 25.99) * mm, v(-1.87, 13.77) * mm, v(2.92, 5.59) * mm, v(-10.1, 7.98) * mm, v(-5.6, 6.1) * mm, v(-0.18, 1.21) * mm, v(3.1, -4.7) * mm, v(6.22, -11.96) * mm, v(7.06, -23.76) * mm, v(4.47, -26.98) * mm, v(3.37, -28.3) * mm]});
            skFitSpline(sketch, "E412.0.3", {"points": [v(-4.98, 52.48) * mm, v(-6.7, 49.75) * mm, v(-10.62, 43.5) * mm, v(-5.88, 25.99) * mm, v(-1.87, 13.77) * mm, v(2.92, 5.59) * mm, v(-10.1, 7.98) * mm, v(-5.6, 6.1) * mm, v(-0.18, 1.21) * mm, v(3.1, -4.7) * mm, v(6.22, -11.96) * mm, v(7.06, -23.76) * mm, v(4.47, -26.98) * mm, v(3.37, -28.3) * mm]});
            skFitSpline(sketch, "E412.0.4", {"points": [v(-4.98, 52.48) * mm, v(-6.7, 49.75) * mm, v(-10.62, 43.5) * mm, v(-5.88, 25.99) * mm, v(-1.87, 13.77) * mm, v(2.92, 5.59) * mm, v(-10.1, 7.98) * mm, v(-5.6, 6.1) * mm, v(-0.18, 1.21) * mm, v(3.1, -4.7) * mm, v(6.22, -11.96) * mm, v(7.06, -23.76) * mm, v(4.47, -26.98) * mm, v(3.37, -28.3) * mm]});
            skFitSpline(sketch, "E412.0.5", {"points": [v(-4.98, 52.48) * mm, v(-6.7, 49.75) * mm, v(-10.62, 43.5) * mm, v(-5.88, 25.99) * mm, v(-1.87, 13.77) * mm, v(2.92, 5.59) * mm, v(-10.1, 7.98) * mm, v(-5.6, 6.1) * mm, v(-0.18, 1.21) * mm, v(3.1, -4.7) * mm, v(6.22, -11.96) * mm, v(7.06, -23.76) * mm, v(4.47, -26.98) * mm, v(3.37, -28.3) * mm]});
            skFitSpline(sketch, "E412.0.6", {"points": [v(3.37, -28.3) * mm, v(2.64, -28.75) * mm, v(0.97, -29.78) * mm, v(-3.9, -28.1) * mm, v(-5.97, -21.21) * mm, v(-5.66, -12.35) * mm, v(-0.94, -0.6) * mm, v(-2.98, -0.7) * mm, v(-5.8, -11.23) * mm, v(-9.45, -25.33) * mm, v(-5.3, -33.23) * mm, v(-1.2, -33.98) * mm, v(2.96, -34.06) * mm, v(6.73, -28.91) * mm, v(8.34, -22.9) * mm, v(7.92, -13.57) * mm, v(3.1, -2.23) * mm, v(-1.5, 5.38) * mm, v(-0.28, 5.14) * mm, v(2.25, 6.15) * mm, v(6.47, 4.82) * mm, v(6.99, 6.4) * mm, v(4.54, 5.76) * mm, v(-3.4, 17.92) * mm, v(-6.87, 34.35) * mm, v(-6.27, 43.3) * mm, v(-5.05, 48.74) * mm, v(-2.39, 51.82) * mm, v(1.15, 51.95) * mm, v(4.34, 51.28) * mm, v(7.11, 46.45) * mm, v(8.14, 37.68) * mm, v(4.93, 25.47) * mm, v(0.5, 14.37) * mm, v(3.53, 15.95) * mm, v(8.93, 37.32) * mm, v(9.2, 47.62) * mm, v(6.74, 54.38) * mm, v(1.93, 56.64) * mm, v(-2.04, 55.26) * mm, v(-4, 53.4) * mm, v(-4.98, 52.48) * mm]});
            skFitSpline(sketch, "E412.0.7", {"points": [v(3.37, -28.3) * mm, v(2.64, -28.75) * mm, v(0.97, -29.78) * mm, v(-3.9, -28.1) * mm, v(-5.97, -21.21) * mm, v(-5.66, -12.35) * mm, v(-0.94, -0.6) * mm, v(-2.98, -0.7) * mm, v(-5.8, -11.23) * mm, v(-9.45, -25.33) * mm, v(-5.3, -33.23) * mm, v(-1.2, -33.98) * mm, v(2.96, -34.06) * mm, v(6.73, -28.91) * mm, v(8.34, -22.9) * mm, v(7.92, -13.57) * mm, v(3.1, -2.23) * mm, v(-1.5, 5.38) * mm, v(-0.28, 5.14) * mm, v(2.25, 6.15) * mm, v(6.47, 4.82) * mm, v(6.99, 6.4) * mm, v(4.54, 5.76) * mm, v(-3.4, 17.92) * mm, v(-6.87, 34.35) * mm, v(-6.27, 43.3) * mm, v(-5.05, 48.74) * mm, v(-2.39, 51.82) * mm, v(1.15, 51.95) * mm, v(4.34, 51.28) * mm, v(7.11, 46.45) * mm, v(8.14, 37.68) * mm, v(4.93, 25.47) * mm, v(0.5, 14.37) * mm, v(3.53, 15.95) * mm, v(8.93, 37.32) * mm, v(9.2, 47.62) * mm, v(6.74, 54.38) * mm, v(1.93, 56.64) * mm, v(-2.04, 55.26) * mm, v(-4, 53.4) * mm, v(-4.98, 52.48) * mm]});
            skFitSpline(sketch, "E412.0.8", {"points": [v(3.37, -28.3) * mm, v(2.64, -28.75) * mm, v(0.97, -29.78) * mm, v(-3.9, -28.1) * mm, v(-5.97, -21.21) * mm, v(-5.66, -12.35) * mm, v(-0.94, -0.6) * mm, v(-2.98, -0.7) * mm, v(-5.8, -11.23) * mm, v(-9.45, -25.33) * mm, v(-5.3, -33.23) * mm, v(-1.2, -33.98) * mm, v(2.96, -34.06) * mm, v(6.73, -28.91) * mm, v(8.34, -22.9) * mm, v(7.92, -13.57) * mm, v(3.1, -2.23) * mm, v(-1.5, 5.38) * mm, v(-0.28, 5.14) * mm, v(2.25, 6.15) * mm, v(6.47, 4.82) * mm, v(6.99, 6.4) * mm, v(4.54, 5.76) * mm, v(-3.4, 17.92) * mm, v(-6.87, 34.35) * mm, v(-6.27, 43.3) * mm, v(-5.05, 48.74) * mm, v(-2.39, 51.82) * mm, v(1.15, 51.95) * mm, v(4.34, 51.28) * mm, v(7.11, 46.45) * mm, v(8.14, 37.68) * mm, v(4.93, 25.47) * mm, v(0.5, 14.37) * mm, v(3.53, 15.95) * mm, v(8.93, 37.32) * mm, v(9.2, 47.62) * mm, v(6.74, 54.38) * mm, v(1.93, 56.64) * mm, v(-2.04, 55.26) * mm, v(-4, 53.4) * mm, v(-4.98, 52.48) * mm]});
            skFitSpline(sketch, "E412.0.9", {"points": [v(3.37, -28.3) * mm, v(2.64, -28.75) * mm, v(0.97, -29.78) * mm, v(-3.9, -28.1) * mm, v(-5.97, -21.21) * mm, v(-5.66, -12.35) * mm, v(-0.94, -0.6) * mm, v(-2.98, -0.7) * mm, v(-5.8, -11.23) * mm, v(-9.45, -25.33) * mm, v(-5.3, -33.23) * mm, v(-1.2, -33.98) * mm, v(2.96, -34.06) * mm, v(6.73, -28.91) * mm, v(8.34, -22.9) * mm, v(7.92, -13.57) * mm, v(3.1, -2.23) * mm, v(-1.5, 5.38) * mm, v(-0.28, 5.14) * mm, v(2.25, 6.15) * mm, v(6.47, 4.82) * mm, v(6.99, 6.4) * mm, v(4.54, 5.76) * mm, v(-3.4, 17.92) * mm, v(-6.87, 34.35) * mm, v(-6.27, 43.3) * mm, v(-5.05, 48.74) * mm, v(-2.39, 51.82) * mm, v(1.15, 51.95) * mm, v(4.34, 51.28) * mm, v(7.11, 46.45) * mm, v(8.14, 37.68) * mm, v(4.93, 25.47) * mm, v(0.5, 14.37) * mm, v(3.53, 15.95) * mm, v(8.93, 37.32) * mm, v(9.2, 47.62) * mm, v(6.74, 54.38) * mm, v(1.93, 56.64) * mm, v(-2.04, 55.26) * mm, v(-4, 53.4) * mm, v(-4.98, 52.48) * mm]});
            skFitSpline(sketch, "E413.0.0", {"points": [v(3.37, -28.3) * mm, v(4.47, -26.98) * mm, v(7.06, -23.76) * mm, v(6.22, -11.96) * mm, v(3.1, -4.7) * mm, v(-0.18, 1.21) * mm, v(-5.6, 6.1) * mm, v(-10.1, 7.98) * mm, v(2.92, 5.59) * mm, v(-1.87, 13.77) * mm, v(-5.88, 25.99) * mm, v(-10.62, 43.5) * mm, v(-6.7, 49.75) * mm, v(-4.98, 52.48) * mm]});
            skLineSegment(sketch, "E413.0.1", {"start": v(-2.02, 7) * mm, "end": v(-3.27, 9.64) * mm});
            skLineSegment(sketch, "E413.0.2", {"start": v(-3.27, 9.64) * mm, "end": v(-7.15, 15.86) * mm});
            skLineSegment(sketch, "E413.0.3", {"start": v(-7.15, 15.86) * mm, "end": v(-8.78, 18.34) * mm});
            skLineSegment(sketch, "E413.0.4", {"start": v(-8.78, 18.34) * mm, "end": v(-10.9, 20.62) * mm});
            skLineSegment(sketch, "E413.0.5", {"start": v(-10.9, 20.62) * mm, "end": v(-12.53, 21.5) * mm});
            skLineSegment(sketch, "E413.0.6", {"start": v(-12.53, 21.5) * mm, "end": v(-13.21, 21.57) * mm});
            skLineSegment(sketch, "E413.0.7", {"start": v(-13.21, 21.57) * mm, "end": v(-13.68, 21.57) * mm});
            skLineSegment(sketch, "E413.0.8", {"start": v(-13.68, 21.57) * mm, "end": v(-13.68, 21.12) * mm});
            skLineSegment(sketch, "E413.0.9", {"start": v(-13.68, 21.12) * mm, "end": v(-13.13, 20.91) * mm});
            skLineSegment(sketch, "E413.0.10", {"start": v(-13.13, 20.91) * mm, "end": v(-12.73, 20.8) * mm});
            skLineSegment(sketch, "E413.0.11", {"start": v(-12.73, 20.8) * mm, "end": v(-12.31, 20.64) * mm});
            skLineSegment(sketch, "E413.0.12", {"start": v(-12.31, 20.64) * mm, "end": v(-11.6, 20.07) * mm});
            skLineSegment(sketch, "E413.0.13", {"start": v(-11.6, 20.07) * mm, "end": v(-10.29, 18.92) * mm});
            skLineSegment(sketch, "E413.0.14", {"start": v(-10.29, 18.92) * mm, "end": v(-9.6, 18.08) * mm});
            skLineSegment(sketch, "E413.0.15", {"start": v(-9.6, 18.08) * mm, "end": v(-7.57, 15.33) * mm});
            skLineSegment(sketch, "E413.0.16", {"start": v(-7.57, 15.33) * mm, "end": v(-7.02, 14.38) * mm});
            skLineSegment(sketch, "E413.0.17", {"start": v(-7.02, 14.38) * mm, "end": v(-7.75, 15.19) * mm});
            skLineSegment(sketch, "E413.0.18", {"start": v(-7.75, 15.19) * mm, "end": v(-8.94, 16.4) * mm});
            skLineSegment(sketch, "E413.0.19", {"start": v(-8.94, 16.4) * mm, "end": v(-9.87, 17.33) * mm});
            skLineSegment(sketch, "E413.0.20", {"start": v(-9.87, 17.33) * mm, "end": v(-10.96, 18.37) * mm});
            skLineSegment(sketch, "E413.0.21", {"start": v(-10.96, 18.37) * mm, "end": v(-12.2, 19.27) * mm});
            skLineSegment(sketch, "E413.0.22", {"start": v(-12.2, 19.27) * mm, "end": v(-13.69, 20.18) * mm});
            skLineSegment(sketch, "E413.0.23", {"start": v(-13.69, 20.18) * mm, "end": v(-14.65, 20.18) * mm});
            skLineSegment(sketch, "E413.0.24", {"start": v(-14.65, 20.18) * mm, "end": v(-15.93, 19.93) * mm});
            skLineSegment(sketch, "E413.0.25", {"start": v(-15.93, 19.93) * mm, "end": v(-16.96, 19.55) * mm});
            skLineSegment(sketch, "E413.0.26", {"start": v(-16.96, 19.55) * mm, "end": v(-17.62, 18.92) * mm});
            skLineSegment(sketch, "E413.0.27", {"start": v(-17.62, 18.92) * mm, "end": v(-18.23, 17.73) * mm});
            skLineSegment(sketch, "E413.0.28", {"start": v(-18.23, 17.73) * mm, "end": v(-18.23, 16.85) * mm});
            skLineSegment(sketch, "E413.0.29", {"start": v(-18.23, 16.85) * mm, "end": v(-17.72, 15.2) * mm});
            skLineSegment(sketch, "E413.0.30", {"start": v(-17.72, 15.2) * mm, "end": v(-17.34, 14.65) * mm});
            skLineSegment(sketch, "E413.0.31", {"start": v(-17.34, 14.65) * mm, "end": v(-16.6, 13.55) * mm});
            skLineSegment(sketch, "E413.0.32", {"start": v(-16.6, 13.55) * mm, "end": v(-15.74, 12.65) * mm});
            skLineSegment(sketch, "E413.0.33", {"start": v(-15.74, 12.65) * mm, "end": v(-14.75, 11.92) * mm});
            skLineSegment(sketch, "E413.0.34", {"start": v(-14.75, 11.92) * mm, "end": v(-13.78, 11.54) * mm});
            skLineSegment(sketch, "E413.0.35", {"start": v(-13.78, 11.54) * mm, "end": v(-12.74, 11.27) * mm});
            skLineSegment(sketch, "E413.0.36", {"start": v(-12.74, 11.27) * mm, "end": v(-11.4, 11.13) * mm});
            skLineSegment(sketch, "E413.0.37", {"start": v(-11.4, 11.13) * mm, "end": v(-11.1, 11.13) * mm});
            skLineSegment(sketch, "E413.0.38", {"start": v(-11.1, 11.13) * mm, "end": v(-10.69, 11.72) * mm});
            skLineSegment(sketch, "E413.0.39", {"start": v(-10.69, 11.72) * mm, "end": v(-11.34, 11.93) * mm});
            skLineSegment(sketch, "E413.0.40", {"start": v(-11.34, 11.93) * mm, "end": v(-11.97, 11.79) * mm});
            skLineSegment(sketch, "E413.0.41", {"start": v(-11.97, 11.79) * mm, "end": v(-13.1, 12.13) * mm});
            skLineSegment(sketch, "E413.0.42", {"start": v(-13.1, 12.13) * mm, "end": v(-13.94, 12.52) * mm});
            skLineSegment(sketch, "E413.0.43", {"start": v(-13.94, 12.52) * mm, "end": v(-14.63, 12.7) * mm});
            skLineSegment(sketch, "E413.0.44", {"start": v(-14.63, 12.7) * mm, "end": v(-15.38, 13.52) * mm});
            skLineSegment(sketch, "E413.0.45", {"start": v(-15.38, 13.52) * mm, "end": v(-16, 13.89) * mm});
            skLineSegment(sketch, "E413.0.46", {"start": v(-16, 13.89) * mm, "end": v(-16.73, 14.92) * mm});
            skLineSegment(sketch, "E413.0.47", {"start": v(-16.73, 14.92) * mm, "end": v(-17.32, 15.96) * mm});
            skLineSegment(sketch, "E413.0.48", {"start": v(-17.32, 15.96) * mm, "end": v(-17.61, 17.2) * mm});
            skLineSegment(sketch, "E413.0.49", {"start": v(-17.61, 17.2) * mm, "end": v(-17.39, 18.18) * mm});
            skLineSegment(sketch, "E413.0.50", {"start": v(-17.39, 18.18) * mm, "end": v(-17.01, 18.74) * mm});
            skLineSegment(sketch, "E413.0.51", {"start": v(-17.01, 18.74) * mm, "end": v(-16.37, 19.15) * mm});
            skLineSegment(sketch, "E413.0.52", {"start": v(-16.37, 19.15) * mm, "end": v(-15.65, 19.46) * mm});
            skLineSegment(sketch, "E413.0.53", {"start": v(-15.65, 19.46) * mm, "end": v(-14.9, 19.65) * mm});
            skLineSegment(sketch, "E413.0.54", {"start": v(-14.9, 19.65) * mm, "end": v(-14.33, 19.65) * mm});
            skLineSegment(sketch, "E413.0.55", {"start": v(-14.33, 19.65) * mm, "end": v(-13.07, 19.2) * mm});
            skLineSegment(sketch, "E413.0.56", {"start": v(-13.07, 19.2) * mm, "end": v(-11.84, 18.16) * mm});
            skLineSegment(sketch, "E413.0.57", {"start": v(-11.84, 18.16) * mm, "end": v(-11.22, 17.7) * mm});
            skLineSegment(sketch, "E413.0.58", {"start": v(-11.22, 17.7) * mm, "end": v(-10.54, 17.07) * mm});
            skLineSegment(sketch, "E413.0.59", {"start": v(-10.54, 17.07) * mm, "end": v(-10.05, 16.63) * mm});
            skLineSegment(sketch, "E413.0.60", {"start": v(-10.05, 16.63) * mm, "end": v(-9.63, 16.2) * mm});
            skLineSegment(sketch, "E413.0.61", {"start": v(-9.63, 16.2) * mm, "end": v(-10.22, 16.58) * mm});
            skLineSegment(sketch, "E413.0.62", {"start": v(-10.22, 16.58) * mm, "end": v(-10.56, 16.83) * mm});
            skLineSegment(sketch, "E413.0.63", {"start": v(-10.56, 16.83) * mm, "end": v(-11.37, 17.3) * mm});
            skLineSegment(sketch, "E413.0.64", {"start": v(-11.37, 17.3) * mm, "end": v(-11.78, 17.53) * mm});
            skLineSegment(sketch, "E413.0.65", {"start": v(-11.78, 17.53) * mm, "end": v(-12.48, 17.88) * mm});
            skLineSegment(sketch, "E413.0.66", {"start": v(-12.48, 17.88) * mm, "end": v(-12.9, 17.84) * mm});
            skLineSegment(sketch, "E413.0.67", {"start": v(-12.9, 17.84) * mm, "end": v(-13.36, 17.87) * mm});
            skLineSegment(sketch, "E413.0.68", {"start": v(-13.36, 17.87) * mm, "end": v(-14, 17.81) * mm});
            skLineSegment(sketch, "E413.0.69", {"start": v(-14, 17.81) * mm, "end": v(-14.47, 17.56) * mm});
            skLineSegment(sketch, "E413.0.70", {"start": v(-14.47, 17.56) * mm, "end": v(-15, 17.2) * mm});
            skLineSegment(sketch, "E413.0.71", {"start": v(-15, 17.2) * mm, "end": v(-15.35, 16.72) * mm});
            skLineSegment(sketch, "E413.0.72", {"start": v(-15.35, 16.72) * mm, "end": v(-15.35, 16.18) * mm});
            skLineSegment(sketch, "E413.0.73", {"start": v(-15.35, 16.18) * mm, "end": v(-15.22, 15.48) * mm});
            skLineSegment(sketch, "E413.0.74", {"start": v(-15.22, 15.48) * mm, "end": v(-14.93, 14.95) * mm});
            skLineSegment(sketch, "E413.0.75", {"start": v(-14.93, 14.95) * mm, "end": v(-14.48, 14.6) * mm});
            skLineSegment(sketch, "E413.0.76", {"start": v(-14.48, 14.6) * mm, "end": v(-13.93, 14.54) * mm});
            skLineSegment(sketch, "E413.0.77", {"start": v(-13.93, 14.54) * mm, "end": v(-13.63, 14.57) * mm});
            skLineSegment(sketch, "E413.0.78", {"start": v(-13.63, 14.57) * mm, "end": v(-13.63, 15.16) * mm});
            skLineSegment(sketch, "E413.0.79", {"start": v(-13.63, 15.16) * mm, "end": v(-14.12, 15.17) * mm});
            skLineSegment(sketch, "E413.0.80", {"start": v(-14.12, 15.17) * mm, "end": v(-14.46, 15.6) * mm});
            skLineSegment(sketch, "E413.0.81", {"start": v(-14.46, 15.6) * mm, "end": v(-14.7, 16.22) * mm});
            skLineSegment(sketch, "E413.0.82", {"start": v(-14.7, 16.22) * mm, "end": v(-14.58, 16.85) * mm});
            skLineSegment(sketch, "E413.0.83", {"start": v(-14.58, 16.85) * mm, "end": v(-14.02, 17.1) * mm});
            skLineSegment(sketch, "E413.0.84", {"start": v(-14.02, 17.1) * mm, "end": v(-13.36, 17.27) * mm});
            skLineSegment(sketch, "E413.0.85", {"start": v(-13.36, 17.27) * mm, "end": v(-12.62, 17.2) * mm});
            skLineSegment(sketch, "E413.0.86", {"start": v(-12.62, 17.2) * mm, "end": v(-11.5, 16.7) * mm});
            skLineSegment(sketch, "E413.0.87", {"start": v(-11.5, 16.7) * mm, "end": v(-10.84, 16.32) * mm});
            skLineSegment(sketch, "E413.0.88", {"start": v(-10.84, 16.32) * mm, "end": v(-9.74, 15.45) * mm});
            skLineSegment(sketch, "E413.0.89", {"start": v(-9.74, 15.45) * mm, "end": v(-8.7, 14.39) * mm});
            skLineSegment(sketch, "E413.0.90", {"start": v(-8.7, 14.39) * mm, "end": v(-7.42, 13.06) * mm});
            skLineSegment(sketch, "E413.0.91", {"start": v(-7.42, 13.06) * mm, "end": v(-6.14, 11.64) * mm});
            skLineSegment(sketch, "E413.0.92", {"start": v(-6.14, 11.64) * mm, "end": v(-5.4, 10.6) * mm});
            skLineSegment(sketch, "E413.0.93", {"start": v(-5.4, 10.6) * mm, "end": v(-5.29, 10.43) * mm});
            skLineSegment(sketch, "E413.0.94", {"start": v(-5.29, 10.43) * mm, "end": v(-4.44, 9.38) * mm});
            skLineSegment(sketch, "E413.0.95", {"start": v(-4.44, 9.38) * mm, "end": v(-3.6, 8.08) * mm});
            skLineSegment(sketch, "E413.0.96", {"start": v(-3.6, 8.08) * mm, "end": v(-2.89, 6.99) * mm});
            skFitSpline(sketch, "E414.0.0", {"points": [v(3.37, -28.3) * mm, v(4.47, -26.98) * mm, v(7.06, -23.76) * mm, v(6.22, -11.96) * mm, v(3.1, -4.7) * mm, v(-0.18, 1.21) * mm, v(-5.6, 6.1) * mm, v(-10.1, 7.98) * mm, v(2.92, 5.59) * mm, v(-1.87, 13.77) * mm, v(-5.88, 25.99) * mm, v(-10.62, 43.5) * mm, v(-6.7, 49.75) * mm, v(-4.98, 52.48) * mm]});
            skLineSegment(sketch, "E415.MirrorCS", {"start": v(2.02, 7) * mm, "end": v(3.27, 9.64) * mm});
            skLineSegment(sketch, "E416.MirrorCS", {"start": v(3.27, 9.64) * mm, "end": v(7.15, 15.86) * mm});
            skLineSegment(sketch, "E417.MirrorCS", {"start": v(7.15, 15.86) * mm, "end": v(8.78, 18.34) * mm});
            skLineSegment(sketch, "E418.MirrorCS", {"start": v(3.6, 8.08) * mm, "end": v(2.89, 6.99) * mm});
            skLineSegment(sketch, "E419.MirrorCS", {"start": v(4.44, 9.38) * mm, "end": v(3.6, 8.08) * mm});
            skLineSegment(sketch, "E420.MirrorCS", {"start": v(5.29, 10.43) * mm, "end": v(4.44, 9.38) * mm});
            skLineSegment(sketch, "E421.MirrorCS", {"start": v(5.4, 10.6) * mm, "end": v(5.29, 10.43) * mm});
            skLineSegment(sketch, "E422.MirrorCS", {"start": v(6.14, 11.64) * mm, "end": v(5.4, 10.6) * mm});
            skLineSegment(sketch, "E423.MirrorCS", {"start": v(12.48, 17.88) * mm, "end": v(12.9, 17.84) * mm});
            skLineSegment(sketch, "E424.MirrorCS", {"start": v(12.62, 17.2) * mm, "end": v(11.5, 16.7) * mm});
            skLineSegment(sketch, "E425.MirrorCS", {"start": v(11.78, 17.53) * mm, "end": v(12.48, 17.88) * mm});
            skLineSegment(sketch, "E426.MirrorCS", {"start": v(11.37, 17.3) * mm, "end": v(11.78, 17.53) * mm});
            skLineSegment(sketch, "E427.MirrorCS", {"start": v(11.84, 18.16) * mm, "end": v(11.22, 17.7) * mm});
            skLineSegment(sketch, "E428.MirrorCS", {"start": v(13.36, 17.27) * mm, "end": v(12.62, 17.2) * mm});
            skLineSegment(sketch, "E429.MirrorCS", {"start": v(10.54, 17.07) * mm, "end": v(10.05, 16.63) * mm});
            skLineSegment(sketch, "E430.MirrorCS", {"start": v(12.9, 17.84) * mm, "end": v(13.36, 17.87) * mm});
            skLineSegment(sketch, "E431.MirrorCS", {"start": v(10.56, 16.83) * mm, "end": v(11.37, 17.3) * mm});
            skLineSegment(sketch, "E432.MirrorCS", {"start": v(11.5, 16.7) * mm, "end": v(10.84, 16.32) * mm});
            skLineSegment(sketch, "E433.MirrorCS", {"start": v(13.36, 17.87) * mm, "end": v(14, 17.81) * mm});
            skLineSegment(sketch, "E434.MirrorCS", {"start": v(14.12, 15.17) * mm, "end": v(14.46, 15.6) * mm});
            skLineSegment(sketch, "E435.MirrorCS", {"start": v(10.22, 16.58) * mm, "end": v(10.56, 16.83) * mm});
            skLineSegment(sketch, "E436.MirrorCS", {"start": v(13.63, 14.57) * mm, "end": v(13.63, 15.16) * mm});
            skLineSegment(sketch, "E437.MirrorCS", {"start": v(9.63, 16.2) * mm, "end": v(10.22, 16.58) * mm});
            skLineSegment(sketch, "E438.MirrorCS", {"start": v(13.93, 14.54) * mm, "end": v(13.63, 14.57) * mm});
            skLineSegment(sketch, "E439.MirrorCS", {"start": v(10.05, 16.63) * mm, "end": v(9.63, 16.2) * mm});
            skLineSegment(sketch, "E440.MirrorCS", {"start": v(12.73, 20.8) * mm, "end": v(12.31, 20.64) * mm});
            skLineSegment(sketch, "E441.MirrorCS", {"start": v(11.22, 17.7) * mm, "end": v(10.54, 17.07) * mm});
            skLineSegment(sketch, "E442.MirrorCS", {"start": v(13.13, 20.91) * mm, "end": v(12.73, 20.8) * mm});
            skLineSegment(sketch, "E443.MirrorCS", {"start": v(15.35, 16.72) * mm, "end": v(15.35, 16.18) * mm});
            skLineSegment(sketch, "E444.MirrorCS", {"start": v(13.68, 21.12) * mm, "end": v(13.13, 20.91) * mm});
            skLineSegment(sketch, "E445.MirrorCS", {"start": v(15, 17.2) * mm, "end": v(15.35, 16.72) * mm});
            skLineSegment(sketch, "E446.MirrorCS", {"start": v(13.69, 20.18) * mm, "end": v(14.65, 20.18) * mm});
            skLineSegment(sketch, "E447.MirrorCS", {"start": v(14.9, 19.65) * mm, "end": v(14.33, 19.65) * mm});
            skLineSegment(sketch, "E448.MirrorCS", {"start": v(14.47, 17.56) * mm, "end": v(15, 17.2) * mm});
            skLineSegment(sketch, "E449.MirrorCS", {"start": v(11.4, 11.13) * mm, "end": v(11.1, 11.13) * mm});
            skLineSegment(sketch, "E450.MirrorCS", {"start": v(15.65, 19.46) * mm, "end": v(14.9, 19.65) * mm});
            skLineSegment(sketch, "E451.MirrorCS", {"start": v(14, 17.81) * mm, "end": v(14.47, 17.56) * mm});
            skLineSegment(sketch, "E452.MirrorCS", {"start": v(16.37, 19.15) * mm, "end": v(15.65, 19.46) * mm});
            skLineSegment(sketch, "E453.MirrorCS", {"start": v(14.02, 17.1) * mm, "end": v(13.36, 17.27) * mm});
            skLineSegment(sketch, "E454.MirrorCS", {"start": v(9.87, 17.33) * mm, "end": v(10.96, 18.37) * mm});
            skLineSegment(sketch, "E455.MirrorCS", {"start": v(14.7, 16.22) * mm, "end": v(14.58, 16.85) * mm});
            skLineSegment(sketch, "E456.MirrorCS", {"start": v(14.58, 16.85) * mm, "end": v(14.02, 17.1) * mm});
            skLineSegment(sketch, "E457.MirrorCS", {"start": v(14.46, 15.6) * mm, "end": v(14.7, 16.22) * mm});
            skLineSegment(sketch, "E458.MirrorCS", {"start": v(13.63, 15.16) * mm, "end": v(14.12, 15.17) * mm});
            skLineSegment(sketch, "E459.MirrorCS", {"start": v(14.48, 14.6) * mm, "end": v(13.93, 14.54) * mm});
            skLineSegment(sketch, "E460.MirrorCS", {"start": v(12.31, 20.64) * mm, "end": v(11.6, 20.07) * mm});
            skLineSegment(sketch, "E461.MirrorCS", {"start": v(14.93, 14.95) * mm, "end": v(14.48, 14.6) * mm});
            skLineSegment(sketch, "E462.MirrorCS", {"start": v(15.22, 15.48) * mm, "end": v(14.93, 14.95) * mm});
            skLineSegment(sketch, "E463.MirrorCS", {"start": v(14.65, 20.18) * mm, "end": v(15.93, 19.93) * mm});
            skLineSegment(sketch, "E464.MirrorCS", {"start": v(13.07, 19.2) * mm, "end": v(11.84, 18.16) * mm});
            skLineSegment(sketch, "E465.MirrorCS", {"start": v(15.35, 16.18) * mm, "end": v(15.22, 15.48) * mm});
            skLineSegment(sketch, "E466.MirrorCS", {"start": v(13.68, 21.57) * mm, "end": v(13.68, 21.12) * mm});
            skLineSegment(sketch, "E467.MirrorCS", {"start": v(14.33, 19.65) * mm, "end": v(13.07, 19.2) * mm});
            skLineSegment(sketch, "E468.MirrorCS", {"start": v(13.21, 21.57) * mm, "end": v(13.68, 21.57) * mm});
            skLineSegment(sketch, "E469.MirrorCS", {"start": v(12.53, 21.5) * mm, "end": v(13.21, 21.57) * mm});
            skLineSegment(sketch, "E470.MirrorCS", {"start": v(12.2, 19.27) * mm, "end": v(13.69, 20.18) * mm});
            skLineSegment(sketch, "E471.MirrorCS", {"start": v(11.1, 11.13) * mm, "end": v(10.69, 11.72) * mm});
            skLineSegment(sketch, "E472.MirrorCS", {"start": v(10.9, 20.62) * mm, "end": v(12.53, 21.5) * mm});
            skLineSegment(sketch, "E473.MirrorCS", {"start": v(10.96, 18.37) * mm, "end": v(12.2, 19.27) * mm});
            skLineSegment(sketch, "E474.MirrorCS", {"start": v(17.39, 18.18) * mm, "end": v(17.01, 18.74) * mm});
            skLineSegment(sketch, "E475.MirrorCS", {"start": v(17.61, 17.2) * mm, "end": v(17.39, 18.18) * mm});
            skLineSegment(sketch, "E476.MirrorCS", {"start": v(16.73, 14.92) * mm, "end": v(17.32, 15.96) * mm});
            skLineSegment(sketch, "E477.MirrorCS", {"start": v(17.34, 14.65) * mm, "end": v(16.6, 13.55) * mm});
            skLineSegment(sketch, "E478.MirrorCS", {"start": v(17.72, 15.2) * mm, "end": v(17.34, 14.65) * mm});
            skLineSegment(sketch, "E479.MirrorCS", {"start": v(16, 13.89) * mm, "end": v(16.73, 14.92) * mm});
            skLineSegment(sketch, "E480.MirrorCS", {"start": v(10.29, 18.92) * mm, "end": v(9.6, 18.08) * mm});
            skLineSegment(sketch, "E481.MirrorCS", {"start": v(15.38, 13.52) * mm, "end": v(16, 13.89) * mm});
            skLineSegment(sketch, "E482.MirrorCS", {"start": v(18.23, 17.73) * mm, "end": v(18.23, 16.85) * mm});
            skLineSegment(sketch, "E483.MirrorCS", {"start": v(14.63, 12.7) * mm, "end": v(15.38, 13.52) * mm});
            skLineSegment(sketch, "E484.MirrorCS", {"start": v(13.94, 12.52) * mm, "end": v(14.63, 12.7) * mm});
            skLineSegment(sketch, "E485.MirrorCS", {"start": v(11.34, 11.93) * mm, "end": v(11.97, 11.79) * mm});
            skLineSegment(sketch, "E486.MirrorCS", {"start": v(11.97, 11.79) * mm, "end": v(13.1, 12.13) * mm});
            skLineSegment(sketch, "E487.MirrorCS", {"start": v(10.69, 11.72) * mm, "end": v(11.34, 11.93) * mm});
            skLineSegment(sketch, "E488.MirrorCS", {"start": v(8.78, 18.34) * mm, "end": v(10.9, 20.62) * mm});
            skLineSegment(sketch, "E489.MirrorCS", {"start": v(12.74, 11.27) * mm, "end": v(11.4, 11.13) * mm});
            skLineSegment(sketch, "E490.MirrorCS", {"start": v(17.01, 18.74) * mm, "end": v(16.37, 19.15) * mm});
            skLineSegment(sketch, "E491.MirrorCS", {"start": v(15.74, 12.65) * mm, "end": v(14.75, 11.92) * mm});
            skLineSegment(sketch, "E492.MirrorCS", {"start": v(14.75, 11.92) * mm, "end": v(13.78, 11.54) * mm});
            skLineSegment(sketch, "E493.MirrorCS", {"start": v(8.94, 16.4) * mm, "end": v(9.87, 17.33) * mm});
            skLineSegment(sketch, "E494.MirrorCS", {"start": v(13.78, 11.54) * mm, "end": v(12.74, 11.27) * mm});
            skLineSegment(sketch, "E495.MirrorCS", {"start": v(16.6, 13.55) * mm, "end": v(15.74, 12.65) * mm});
            skLineSegment(sketch, "E496.MirrorCS", {"start": v(17.32, 15.96) * mm, "end": v(17.61, 17.2) * mm});
            skLineSegment(sketch, "E497.MirrorCS", {"start": v(18.23, 16.85) * mm, "end": v(17.72, 15.2) * mm});
            skLineSegment(sketch, "E498.MirrorCS", {"start": v(11.6, 20.07) * mm, "end": v(10.29, 18.92) * mm});
            skLineSegment(sketch, "E499.MirrorCS", {"start": v(17.62, 18.92) * mm, "end": v(18.23, 17.73) * mm});
            skLineSegment(sketch, "E500.MirrorCS", {"start": v(16.96, 19.55) * mm, "end": v(17.62, 18.92) * mm});
            skLineSegment(sketch, "E501.MirrorCS", {"start": v(13.1, 12.13) * mm, "end": v(13.94, 12.52) * mm});
            skLineSegment(sketch, "E502.MirrorCS", {"start": v(10.84, 16.32) * mm, "end": v(9.74, 15.45) * mm});
            skLineSegment(sketch, "E503.MirrorCS", {"start": v(9.74, 15.45) * mm, "end": v(8.7, 14.39) * mm});
            skLineSegment(sketch, "E504.MirrorCS", {"start": v(15.93, 19.93) * mm, "end": v(16.96, 19.55) * mm});
            skLineSegment(sketch, "E505.MirrorCS", {"start": v(7.42, 13.06) * mm, "end": v(6.14, 11.64) * mm});
            skLineSegment(sketch, "E506.MirrorCS", {"start": v(8.7, 14.39) * mm, "end": v(7.42, 13.06) * mm});
            skLineSegment(sketch, "E507.MirrorCS", {"start": v(9.6, 18.08) * mm, "end": v(7.57, 15.33) * mm});
            skLineSegment(sketch, "E508.MirrorCS", {"start": v(7.75, 15.19) * mm, "end": v(8.94, 16.4) * mm});
            skLineSegment(sketch, "E509.MirrorCS", {"start": v(7.57, 15.33) * mm, "end": v(7.02, 14.38) * mm});
            skLineSegment(sketch, "E510.MirrorCS", {"start": v(7.02, 14.38) * mm, "end": v(7.75, 15.19) * mm});
            skLineSegment(sketch, "E511", {"start": v(0, 6.4) * mm, "end": v(24.48, 6.4) * mm, "construction": true});
            skLineSegment(sketch, "E512.MirrorCS", {"start": v(3.6, 4.7) * mm, "end": v(3, 5.63) * mm});
            skLineSegment(sketch, "E513.MirrorCS", {"start": v(2.08, 5.67) * mm, "end": v(3.27, 3.14) * mm});
            skLineSegment(sketch, "E514.MirrorCS", {"start": v(4.44, 3.4) * mm, "end": v(3.6, 4.7) * mm});
            skLineSegment(sketch, "E515.MirrorCS", {"start": v(3.27, 3.14) * mm, "end": v(7.15, -3.08) * mm});
            skLineSegment(sketch, "E516.MirrorCS", {"start": v(5.29, 2.35) * mm, "end": v(4.44, 3.4) * mm});
            skLineSegment(sketch, "E517.MirrorCS", {"start": v(5.4, 2.18) * mm, "end": v(5.29, 2.35) * mm});
            skLineSegment(sketch, "E518.MirrorCS", {"start": v(6.14, 1.14) * mm, "end": v(5.4, 2.18) * mm});
            skLineSegment(sketch, "E519.MirrorCS", {"start": v(7.42, -0.28) * mm, "end": v(6.14, 1.14) * mm});
            skLineSegment(sketch, "E520.MirrorCS", {"start": v(12.9, -5.06) * mm, "end": v(13.36, -5.09) * mm});
            skLineSegment(sketch, "E521.MirrorCS", {"start": v(12.48, -5.1) * mm, "end": v(12.9, -5.06) * mm});
            skLineSegment(sketch, "E522.MirrorCS", {"start": v(13.63, -1.79) * mm, "end": v(13.63, -2.38) * mm});
            skLineSegment(sketch, "E523.MirrorCS", {"start": v(13.69, -7.4) * mm, "end": v(14.65, -7.4) * mm});
            skLineSegment(sketch, "E524.MirrorCS", {"start": v(13.63, -2.38) * mm, "end": v(14.12, -2.38) * mm});
            skLineSegment(sketch, "E525.MirrorCS", {"start": v(14.93, -2.17) * mm, "end": v(14.48, -1.82) * mm});
            skLineSegment(sketch, "E526.MirrorCS", {"start": v(10.56, -4.04) * mm, "end": v(11.37, -4.52) * mm});
            skLineSegment(sketch, "E527.MirrorCS", {"start": v(14.12, -2.38) * mm, "end": v(14.46, -2.81) * mm});
            skLineSegment(sketch, "E528.MirrorCS", {"start": v(10.22, -3.8) * mm, "end": v(10.56, -4.04) * mm});
            skLineSegment(sketch, "E529.MirrorCS", {"start": v(14.46, -2.81) * mm, "end": v(14.7, -3.44) * mm});
            skLineSegment(sketch, "E530.MirrorCS", {"start": v(11.5, -3.92) * mm, "end": v(10.84, -3.54) * mm});
            skLineSegment(sketch, "E531.MirrorCS", {"start": v(13.36, -4.5) * mm, "end": v(12.62, -4.43) * mm});
            skLineSegment(sketch, "E532.MirrorCS", {"start": v(12.31, -7.85) * mm, "end": v(11.6, -7.28) * mm});
            skLineSegment(sketch, "E533.MirrorCS", {"start": v(14.02, -4.32) * mm, "end": v(13.36, -4.5) * mm});
            skLineSegment(sketch, "E534.MirrorCS", {"start": v(13.36, -5.09) * mm, "end": v(14, -5.03) * mm});
            skLineSegment(sketch, "E535.MirrorCS", {"start": v(9.63, -3.42) * mm, "end": v(10.22, -3.8) * mm});
            skLineSegment(sketch, "E536.MirrorCS", {"start": v(11.78, -4.75) * mm, "end": v(12.48, -5.1) * mm});
            skLineSegment(sketch, "E537.MirrorCS", {"start": v(15.35, -3.93) * mm, "end": v(15.35, -3.4) * mm});
            skLineSegment(sketch, "E538.MirrorCS", {"start": v(13.93, -1.75) * mm, "end": v(13.63, -1.79) * mm});
            skLineSegment(sketch, "E539.MirrorCS", {"start": v(11.37, -4.52) * mm, "end": v(11.78, -4.75) * mm});
            skLineSegment(sketch, "E540.MirrorCS", {"start": v(10.05, -3.84) * mm, "end": v(9.63, -3.42) * mm});
            skLineSegment(sketch, "E541.MirrorCS", {"start": v(12.73, -8) * mm, "end": v(12.31, -7.85) * mm});
            skLineSegment(sketch, "E542.MirrorCS", {"start": v(14.7, -3.44) * mm, "end": v(14.58, -4.07) * mm});
            skLineSegment(sketch, "E543.MirrorCS", {"start": v(15.22, -2.7) * mm, "end": v(14.93, -2.17) * mm});
            skLineSegment(sketch, "E544.MirrorCS", {"start": v(14.33, -6.87) * mm, "end": v(13.07, -6.4) * mm});
            skLineSegment(sketch, "E545.MirrorCS", {"start": v(14.48, -1.82) * mm, "end": v(13.93, -1.75) * mm});
            skLineSegment(sketch, "E546.MirrorCS", {"start": v(13.07, -6.4) * mm, "end": v(11.84, -5.38) * mm});
            skLineSegment(sketch, "E547.MirrorCS", {"start": v(13.13, -8.13) * mm, "end": v(12.73, -8) * mm});
            skLineSegment(sketch, "E548.MirrorCS", {"start": v(12.2, -6.49) * mm, "end": v(13.69, -7.4) * mm});
            skLineSegment(sketch, "E549.MirrorCS", {"start": v(11.22, -4.92) * mm, "end": v(10.54, -4.28) * mm});
            skLineSegment(sketch, "E550.MirrorCS", {"start": v(10.54, -4.28) * mm, "end": v(10.05, -3.84) * mm});
            skLineSegment(sketch, "E551.MirrorCS", {"start": v(15.35, -3.4) * mm, "end": v(15.22, -2.7) * mm});
            skLineSegment(sketch, "E552.MirrorCS", {"start": v(10.84, -3.54) * mm, "end": v(9.74, -2.66) * mm});
            skLineSegment(sketch, "E553.MirrorCS", {"start": v(12.53, -8.72) * mm, "end": v(13.21, -8.79) * mm});
            skLineSegment(sketch, "E554.MirrorCS", {"start": v(12.62, -4.43) * mm, "end": v(11.5, -3.92) * mm});
            skLineSegment(sketch, "E555.MirrorCS", {"start": v(14.9, -6.87) * mm, "end": v(14.33, -6.87) * mm});
            skLineSegment(sketch, "E556.MirrorCS", {"start": v(14.58, -4.07) * mm, "end": v(14.02, -4.32) * mm});
            skLineSegment(sketch, "E557.MirrorCS", {"start": v(14.47, -4.78) * mm, "end": v(15, -4.42) * mm});
            skLineSegment(sketch, "E558.MirrorCS", {"start": v(11.84, -5.38) * mm, "end": v(11.22, -4.92) * mm});
            skLineSegment(sketch, "E559.MirrorCS", {"start": v(13.68, -8.34) * mm, "end": v(13.13, -8.13) * mm});
            skLineSegment(sketch, "E560.MirrorCS", {"start": v(14, -5.03) * mm, "end": v(14.47, -4.78) * mm});
            skLineSegment(sketch, "E561.MirrorCS", {"start": v(13.21, -8.79) * mm, "end": v(13.68, -8.79) * mm});
            skLineSegment(sketch, "E562.MirrorCS", {"start": v(10.69, 1.06) * mm, "end": v(11.34, 0.85) * mm});
            skLineSegment(sketch, "E563.MirrorCS", {"start": v(11.1, 1.66) * mm, "end": v(10.69, 1.06) * mm});
            skLineSegment(sketch, "E564.MirrorCS", {"start": v(13.68, -8.79) * mm, "end": v(13.68, -8.34) * mm});
            skLineSegment(sketch, "E565.MirrorCS", {"start": v(15.38, -0.74) * mm, "end": v(16, -1.1) * mm});
            skLineSegment(sketch, "E566.MirrorCS", {"start": v(9.87, -4.55) * mm, "end": v(10.96, -5.59) * mm});
            skLineSegment(sketch, "E567.MirrorCS", {"start": v(11.34, 0.85) * mm, "end": v(11.97, 1) * mm});
            skLineSegment(sketch, "E568.MirrorCS", {"start": v(10.9, -7.83) * mm, "end": v(12.53, -8.72) * mm});
            skLineSegment(sketch, "E569.MirrorCS", {"start": v(10.96, -5.59) * mm, "end": v(12.2, -6.49) * mm});
            skLineSegment(sketch, "E570.MirrorCS", {"start": v(12.74, 1.5) * mm, "end": v(11.4, 1.66) * mm});
            skLineSegment(sketch, "E571.MirrorCS", {"start": v(11.4, 1.66) * mm, "end": v(11.1, 1.66) * mm});
            skLineSegment(sketch, "E572.MirrorCS", {"start": v(8.94, -3.62) * mm, "end": v(9.87, -4.55) * mm});
            skLineSegment(sketch, "E573.MirrorCS", {"start": v(14.65, -7.4) * mm, "end": v(15.93, -7.15) * mm});
            skLineSegment(sketch, "E574.MirrorCS", {"start": v(15.65, -6.68) * mm, "end": v(14.9, -6.87) * mm});
            skLineSegment(sketch, "E575.MirrorCS", {"start": v(17.62, -6.14) * mm, "end": v(18.23, -4.95) * mm});
            skLineSegment(sketch, "E576.MirrorCS", {"start": v(10.29, -6.14) * mm, "end": v(9.6, -5.3) * mm});
            skLineSegment(sketch, "E577.MirrorCS", {"start": v(15, -4.42) * mm, "end": v(15.35, -3.93) * mm});
            skLineSegment(sketch, "E578.MirrorCS", {"start": v(16.96, -6.76) * mm, "end": v(17.62, -6.14) * mm});
            skLineSegment(sketch, "E579.MirrorCS", {"start": v(17.72, -2.42) * mm, "end": v(17.34, -1.87) * mm});
            skLineSegment(sketch, "E580.MirrorCS", {"start": v(16.37, -6.37) * mm, "end": v(15.65, -6.68) * mm});
            skLineSegment(sketch, "E581.MirrorCS", {"start": v(13.1, 0.65) * mm, "end": v(13.94, 0.27) * mm});
            skLineSegment(sketch, "E582.MirrorCS", {"start": v(16, -1.1) * mm, "end": v(16.73, -2.13) * mm});
            skLineSegment(sketch, "E583.MirrorCS", {"start": v(18.23, -4.95) * mm, "end": v(18.23, -4.07) * mm});
            skLineSegment(sketch, "E584.MirrorCS", {"start": v(14.63, 0.09) * mm, "end": v(15.38, -0.74) * mm});
            skLineSegment(sketch, "E585.MirrorCS", {"start": v(17.39, -5.4) * mm, "end": v(17.01, -5.95) * mm});
            skLineSegment(sketch, "E586.MirrorCS", {"start": v(15.93, -7.15) * mm, "end": v(16.96, -6.76) * mm});
            skLineSegment(sketch, "E587.MirrorCS", {"start": v(18.23, -4.07) * mm, "end": v(17.72, -2.42) * mm});
            skLineSegment(sketch, "E588.MirrorCS", {"start": v(13.94, 0.27) * mm, "end": v(14.63, 0.09) * mm});
            skLineSegment(sketch, "E589.MirrorCS", {"start": v(13.78, 1.24) * mm, "end": v(12.74, 1.5) * mm});
            skLineSegment(sketch, "E590.MirrorCS", {"start": v(17.34, -1.87) * mm, "end": v(16.6, -0.76) * mm});
            skLineSegment(sketch, "E591.MirrorCS", {"start": v(17.32, -3.18) * mm, "end": v(17.61, -4.43) * mm});
            skLineSegment(sketch, "E592.MirrorCS", {"start": v(16.6, -0.76) * mm, "end": v(15.74, 0.13) * mm});
            skLineSegment(sketch, "E593.MirrorCS", {"start": v(16.73, -2.13) * mm, "end": v(17.32, -3.18) * mm});
            skLineSegment(sketch, "E594.MirrorCS", {"start": v(11.97, 1) * mm, "end": v(13.1, 0.65) * mm});
            skLineSegment(sketch, "E595.MirrorCS", {"start": v(14.75, 0.86) * mm, "end": v(13.78, 1.24) * mm});
            skLineSegment(sketch, "E596.MirrorCS", {"start": v(17.61, -4.43) * mm, "end": v(17.39, -5.4) * mm});
            skLineSegment(sketch, "E597.MirrorCS", {"start": v(15.74, 0.13) * mm, "end": v(14.75, 0.86) * mm});
            skLineSegment(sketch, "E598.MirrorCS", {"start": v(11.6, -7.28) * mm, "end": v(10.29, -6.14) * mm});
            skLineSegment(sketch, "E599.MirrorCS", {"start": v(17.01, -5.95) * mm, "end": v(16.37, -6.37) * mm});
            skLineSegment(sketch, "E600.MirrorCS", {"start": v(9.74, -2.66) * mm, "end": v(8.7, -1.6) * mm});
            skLineSegment(sketch, "E601.MirrorCS", {"start": v(8.7, -1.6) * mm, "end": v(7.42, -0.28) * mm});
            skLineSegment(sketch, "E602.MirrorCS", {"start": v(7.02, -1.6) * mm, "end": v(7.75, -2.4) * mm});
            skLineSegment(sketch, "E603.MirrorCS", {"start": v(7.75, -2.4) * mm, "end": v(8.94, -3.62) * mm});
            skLineSegment(sketch, "E604.MirrorCS", {"start": v(9.6, -5.3) * mm, "end": v(7.57, -2.55) * mm});
            skLineSegment(sketch, "E605.MirrorCS", {"start": v(8.78, -5.56) * mm, "end": v(10.9, -7.83) * mm});
            skLineSegment(sketch, "E606.MirrorCS", {"start": v(7.15, -3.08) * mm, "end": v(8.78, -5.56) * mm});
            skLineSegment(sketch, "E607.MirrorCS", {"start": v(7.57, -2.55) * mm, "end": v(7.02, -1.6) * mm});
            skPoint(sketch, "E608.orphan", {"position": v(2.02, 5.79) * mm});
            skPoint(sketch, "E609.orphan", {"position": v(2.89, 5.8) * mm});
            skFitSpline(sketch, "E610.0.0", {"points": [v(3.37, -28.3) * mm, v(4.47, -26.98) * mm, v(7.06, -23.76) * mm, v(6.22, -11.96) * mm, v(3.1, -4.7) * mm, v(-0.18, 1.21) * mm, v(-5.6, 6.1) * mm, v(-10.1, 7.98) * mm, v(2.92, 5.59) * mm, v(-1.87, 13.77) * mm, v(-5.88, 25.99) * mm, v(-10.62, 43.5) * mm, v(-6.7, 49.75) * mm, v(-4.98, 52.48) * mm]});
            skLineSegment(sketch, "E610.0.1", {"start": v(-3.23, 3.82) * mm, "end": v(-3.53, 2.65) * mm});
            skLineSegment(sketch, "E610.0.2", {"start": v(-3.53, 2.65) * mm, "end": v(-4.67, 0) * mm});
            skLineSegment(sketch, "E610.0.3", {"start": v(-4.67, 0) * mm, "end": v(-5.32, -1.28) * mm});
            skLineSegment(sketch, "E610.0.4", {"start": v(-5.32, -1.28) * mm, "end": v(-5.98, -2.28) * mm});
            skLineSegment(sketch, "E610.0.5", {"start": v(-5.98, -2.28) * mm, "end": v(-6.87, -3.36) * mm});
            skLineSegment(sketch, "E610.0.6", {"start": v(-6.87, -3.36) * mm, "end": v(-7.87, -4.23) * mm});
            skLineSegment(sketch, "E610.0.7", {"start": v(-7.87, -4.23) * mm, "end": v(-8.32, -4.54) * mm});
            skLineSegment(sketch, "E610.0.8", {"start": v(-8.32, -4.54) * mm, "end": v(-9.22, -4.74) * mm});
            skLineSegment(sketch, "E610.0.9", {"start": v(-9.22, -4.74) * mm, "end": v(-10.16, -4.74) * mm});
            skLineSegment(sketch, "E610.0.10", {"start": v(-10.16, -4.74) * mm, "end": v(-10.42, -4.36) * mm});
            skLineSegment(sketch, "E610.0.11", {"start": v(-10.42, -4.36) * mm, "end": v(-10.42, -3.71) * mm});
            skLineSegment(sketch, "E610.0.12", {"start": v(-10.42, -3.71) * mm, "end": v(-10.63, -3.43) * mm});
            skLineSegment(sketch, "E610.0.13", {"start": v(-10.63, -3.43) * mm, "end": v(-10.45, -2.6) * mm});
            skLineSegment(sketch, "E610.0.14", {"start": v(-10.45, -2.6) * mm, "end": v(-10.54, -2.17) * mm});
            skLineSegment(sketch, "E610.0.15", {"start": v(-10.54, -2.17) * mm, "end": v(-10.74, -2.06) * mm});
            skLineSegment(sketch, "E610.0.16", {"start": v(-10.74, -2.06) * mm, "end": v(-11.05, -2.06) * mm});
            skLineSegment(sketch, "E610.0.17", {"start": v(-11.05, -2.06) * mm, "end": v(-11.3, -2.67) * mm});
            skLineSegment(sketch, "E610.0.18", {"start": v(-11.3, -2.67) * mm, "end": v(-11.31, -3.32) * mm});
            skLineSegment(sketch, "E610.0.19", {"start": v(-11.31, -3.32) * mm, "end": v(-11.38, -4.27) * mm});
            skLineSegment(sketch, "E610.0.20", {"start": v(-11.38, -4.27) * mm, "end": v(-11.1, -4.7) * mm});
            skLineSegment(sketch, "E610.0.21", {"start": v(-11.1, -4.7) * mm, "end": v(-10.84, -5.13) * mm});
            skLineSegment(sketch, "E610.0.22", {"start": v(-10.84, -5.13) * mm, "end": v(-10.2, -5.45) * mm});
            skLineSegment(sketch, "E610.0.23", {"start": v(-10.2, -5.45) * mm, "end": v(-9.22, -5.45) * mm});
            skLineSegment(sketch, "E610.0.24", {"start": v(-9.22, -5.45) * mm, "end": v(-8.63, -5.4) * mm});
            skLineSegment(sketch, "E610.0.25", {"start": v(-8.63, -5.4) * mm, "end": v(-8.1, -5.4) * mm});
            skLineSegment(sketch, "E610.0.26", {"start": v(-8.1, -5.4) * mm, "end": v(-7.24, -4.56) * mm});
            skLineSegment(sketch, "E610.0.27", {"start": v(-7.24, -4.56) * mm, "end": v(-6.54, -3.72) * mm});
            skLineSegment(sketch, "E610.0.28", {"start": v(-6.54, -3.72) * mm, "end": v(-6.03, -3.34) * mm});
            skLineSegment(sketch, "E610.0.29", {"start": v(-6.03, -3.34) * mm, "end": v(-6.5, -4.46) * mm});
            skLineSegment(sketch, "E610.0.30", {"start": v(-6.5, -4.46) * mm, "end": v(-7.07, -5.24) * mm});
            skLineSegment(sketch, "E610.0.31", {"start": v(-7.07, -5.24) * mm, "end": v(-7.52, -6.04) * mm});
            skLineSegment(sketch, "E610.0.32", {"start": v(-7.52, -6.04) * mm, "end": v(-8.32, -7.05) * mm});
            skLineSegment(sketch, "E610.0.33", {"start": v(-8.32, -7.05) * mm, "end": v(-9.24, -7.65) * mm});
            skLineSegment(sketch, "E610.0.34", {"start": v(-9.24, -7.65) * mm, "end": v(-10.41, -7.9) * mm});
            skLineSegment(sketch, "E610.0.35", {"start": v(-10.41, -7.9) * mm, "end": v(-11.4, -7.9) * mm});
            skLineSegment(sketch, "E610.0.36", {"start": v(-11.4, -7.9) * mm, "end": v(-12.18, -7.9) * mm});
            skLineSegment(sketch, "E610.0.37", {"start": v(-12.18, -7.9) * mm, "end": v(-12.86, -7.3) * mm});
            skLineSegment(sketch, "E610.0.38", {"start": v(-12.86, -7.3) * mm, "end": v(-13.25, -6.73) * mm});
            skLineSegment(sketch, "E610.0.39", {"start": v(-13.25, -6.73) * mm, "end": v(-13.4, -5.68) * mm});
            skLineSegment(sketch, "E610.0.40", {"start": v(-13.4, -5.68) * mm, "end": v(-13.43, -4.14) * mm});
            skLineSegment(sketch, "E610.0.41", {"start": v(-13.43, -4.14) * mm, "end": v(-13.19, -2.86) * mm});
            skLineSegment(sketch, "E610.0.42", {"start": v(-13.19, -2.86) * mm, "end": v(-12.68, -1.8) * mm});
            skLineSegment(sketch, "E610.0.43", {"start": v(-12.68, -1.8) * mm, "end": v(-11.68, -0.78) * mm});
            skLineSegment(sketch, "E610.0.44", {"start": v(-11.68, -0.78) * mm, "end": v(-10.65, 0) * mm});
            skLineSegment(sketch, "E610.0.45", {"start": v(-10.65, 0) * mm, "end": v(-9.85, 0.55) * mm});
            skLineSegment(sketch, "E610.0.46", {"start": v(-9.85, 0.55) * mm, "end": v(-9.48, 0.86) * mm});
            skLineSegment(sketch, "E610.0.47", {"start": v(-9.48, 0.86) * mm, "end": v(-8.95, 0.86) * mm});
            skLineSegment(sketch, "E610.0.48", {"start": v(-8.95, 0.86) * mm, "end": v(-8.37, 1.21) * mm});
            skLineSegment(sketch, "E610.0.49", {"start": v(-8.37, 1.21) * mm, "end": v(-8.58, 1.52) * mm});
            skLineSegment(sketch, "E610.0.50", {"start": v(-8.58, 1.52) * mm, "end": v(-9.6, 1.97) * mm});
            skLineSegment(sketch, "E610.0.51", {"start": v(-9.6, 1.97) * mm, "end": v(-10.5, 1.2) * mm});
            skLineSegment(sketch, "E610.0.52", {"start": v(-10.5, 1.2) * mm, "end": v(-10.84, 1.2) * mm});
            skLineSegment(sketch, "E610.0.53", {"start": v(-10.84, 1.2) * mm, "end": v(-11.37, 0.56) * mm});
            skLineSegment(sketch, "E610.0.54", {"start": v(-11.37, 0.56) * mm, "end": v(-12.27, -0.35) * mm});
            skLineSegment(sketch, "E610.0.55", {"start": v(-12.27, -0.35) * mm, "end": v(-13.01, -1.03) * mm});
            skLineSegment(sketch, "E610.0.56", {"start": v(-13.01, -1.03) * mm, "end": v(-13.62, -2.1) * mm});
            skLineSegment(sketch, "E610.0.57", {"start": v(-13.62, -2.1) * mm, "end": v(-13.85, -2.41) * mm});
            skLineSegment(sketch, "E610.0.58", {"start": v(-13.85, -2.41) * mm, "end": v(-14.03, -3.05) * mm});
            skLineSegment(sketch, "E610.0.59", {"start": v(-14.03, -3.05) * mm, "end": v(-14.23, -4.16) * mm});
            skLineSegment(sketch, "E610.0.60", {"start": v(-14.23, -4.16) * mm, "end": v(-14.2, -5.04) * mm});
            skLineSegment(sketch, "E610.0.61", {"start": v(-14.2, -5.04) * mm, "end": v(-14.2, -6.57) * mm});
            skLineSegment(sketch, "E610.0.62", {"start": v(-14.2, -6.57) * mm, "end": v(-13.8, -7.26) * mm});
            skLineSegment(sketch, "E610.0.63", {"start": v(-13.8, -7.26) * mm, "end": v(-13.1, -8.04) * mm});
            skLineSegment(sketch, "E610.0.64", {"start": v(-13.1, -8.04) * mm, "end": v(-12.11, -8.5) * mm});
            skLineSegment(sketch, "E610.0.65", {"start": v(-12.11, -8.5) * mm, "end": v(-11.1, -8.71) * mm});
            skLineSegment(sketch, "E610.0.66", {"start": v(-11.1, -8.71) * mm, "end": v(-10.08, -8.52) * mm});
            skLineSegment(sketch, "E610.0.67", {"start": v(-10.08, -8.52) * mm, "end": v(-9.26, -8.33) * mm});
            skLineSegment(sketch, "E610.0.68", {"start": v(-9.26, -8.33) * mm, "end": v(-8.46, -7.7) * mm});
            skLineSegment(sketch, "E610.0.69", {"start": v(-8.46, -7.7) * mm, "end": v(-7.54, -7.03) * mm});
            skLineSegment(sketch, "E610.0.70", {"start": v(-7.54, -7.03) * mm, "end": v(-7, -6.3) * mm});
            skLineSegment(sketch, "E610.0.71", {"start": v(-7, -6.3) * mm, "end": v(-6.41, -5.36) * mm});
            skLineSegment(sketch, "E610.0.72", {"start": v(-6.41, -5.36) * mm, "end": v(-5.9, -4.6) * mm});
            skLineSegment(sketch, "E610.0.73", {"start": v(-5.9, -4.6) * mm, "end": v(-5.43, -3.59) * mm});
            skLineSegment(sketch, "E610.0.74", {"start": v(-5.43, -3.59) * mm, "end": v(-5.76, -4.64) * mm});
            skLineSegment(sketch, "E610.0.75", {"start": v(-5.76, -4.64) * mm, "end": v(-6.14, -5.8) * mm});
            skLineSegment(sketch, "E610.0.76", {"start": v(-6.14, -5.8) * mm, "end": v(-6.77, -6.99) * mm});
            skLineSegment(sketch, "E610.0.77", {"start": v(-6.77, -6.99) * mm, "end": v(-7.57, -7.8) * mm});
            skLineSegment(sketch, "E610.0.78", {"start": v(-7.57, -7.8) * mm, "end": v(-8.08, -8.55) * mm});
            skLineSegment(sketch, "E610.0.79", {"start": v(-8.08, -8.55) * mm, "end": v(-8.56, -8.84) * mm});
            skLineSegment(sketch, "E610.0.80", {"start": v(-8.56, -8.84) * mm, "end": v(-9.27, -8.85) * mm});
            skLineSegment(sketch, "E610.0.81", {"start": v(-9.27, -8.85) * mm, "end": v(-9.78, -9.25) * mm});
            skLineSegment(sketch, "E610.0.82", {"start": v(-9.78, -9.25) * mm, "end": v(-10.6, -9.5) * mm});
            skLineSegment(sketch, "E610.0.83", {"start": v(-10.6, -9.5) * mm, "end": v(-11.1, -9.74) * mm});
            skLineSegment(sketch, "E610.0.84", {"start": v(-11.1, -9.74) * mm, "end": v(-10.96, -10) * mm});
            skLineSegment(sketch, "E610.0.85", {"start": v(-10.96, -10) * mm, "end": v(-10.5, -9.91) * mm});
            skLineSegment(sketch, "E610.0.86", {"start": v(-10.5, -9.91) * mm, "end": v(-9.74, -9.91) * mm});
            skLineSegment(sketch, "E610.0.87", {"start": v(-9.74, -9.91) * mm, "end": v(-9.23, -9.6) * mm});
            skLineSegment(sketch, "E610.0.88", {"start": v(-9.23, -9.6) * mm, "end": v(-8.32, -9.37) * mm});
            skLineSegment(sketch, "E610.0.89", {"start": v(-8.32, -9.37) * mm, "end": v(-7.69, -9.14) * mm});
            skLineSegment(sketch, "E610.0.90", {"start": v(-7.69, -9.14) * mm, "end": v(-6.89, -8.03) * mm});
            skLineSegment(sketch, "E610.0.91", {"start": v(-6.89, -8.03) * mm, "end": v(-6.24, -7.18) * mm});
            skLineSegment(sketch, "E610.0.92", {"start": v(-6.24, -7.18) * mm, "end": v(-5.7, -6.27) * mm});
            skLineSegment(sketch, "E610.0.93", {"start": v(-5.7, -6.27) * mm, "end": v(-5.2, -5.16) * mm});
            skLineSegment(sketch, "E610.0.94", {"start": v(-5.2, -5.16) * mm, "end": v(-4.53, -3.14) * mm});
            skLineSegment(sketch, "E610.0.95", {"start": v(-4.53, -3.14) * mm, "end": v(-3.9, -1.64) * mm});
            skLineSegment(sketch, "E610.0.96", {"start": v(-3.9, -1.64) * mm, "end": v(-3.49, -0.28) * mm});
            skLineSegment(sketch, "E610.0.97", {"start": v(-3.49, -0.28) * mm, "end": v(-2.97, 1.56) * mm});
            skLineSegment(sketch, "E610.0.98", {"start": v(-2.97, 1.56) * mm, "end": v(-2.4, 3.03) * mm});
            skCircle(sketch, "E611", {"center": v(1.63, 58.47) * mm, "radius": 2.4 * mm});
            skPoint(sketch, "E611.first.point", {"position": v(1.7, 56.07) * mm});
            skPoint(sketch, "E611.second.point", {"position": v(1.58, 60.87) * mm});
            skPoint(sketch, "E611.third.point", {"position": v(4, 58.87) * mm});
            skLineSegment(sketch, "E612", {"start": v(-0.8, 58.38) * mm, "end": v(3.98, 58.5) * mm, "construction": true});
            skCircle(sketch, "E613", {"center": v(1.64, 58.46) * mm, "radius": 1.4 * mm});
            skSolve(sketch);
        }
        {
            var Q0;
            {var subQ0=sQuery(id+"F0.wireOp",EDGE,"E0");var subQ4=sQuery(id+"F0.wireOp",EDGE,"E1");var subQ5=makeQuery(id+"F0.imprint","INTERSECT",VERTEX,{"disambiguationData":[OD(0.0)],"derivedFrom":[subQ0,subQ4]});Q0=makeQuery(id+"F0.imprint","IMPRINT",FACE,{"disambiguationData":[TD([[makeQuery(id+"F0.imprint","IMPRINT",EDGE,{"disambiguationData":[TD([[subQ5,-1.0]])],"derivedFrom":subQ0}),1.0]])]});}
            var Q1;
            {var subQ0=sQuery(id+"F0.wireOp",EDGE,"E2");Q1=makeQuery(id+"F0.imprint","IMPRINT",FACE,{"disambiguationData":[TD([[makeQuery(id+"F0.imprint","IMPRINT",EDGE,{"derivedFrom":subQ0}),1.0]])]});}
            var Q2;
            {var subQ1=sQuery(id+"F1.wireOp",EDGE,"E416.MirrorCS");Q2=makeQuery(id+"F1.imprint","IMPRINT",FACE,{"disambiguationData":[TD([[makeQuery(id+"F1.imprint","IMPRINT",EDGE,{"derivedFrom":subQ1}),-1.0]])]});}
            var Q3;
            {var subQ3=sQuery(id+"F1.wireOp",EDGE,"E512.MirrorCS");Q3=makeQuery(id+"F1.imprint","IMPRINT",FACE,{"disambiguationData":[TD([[makeQuery(id+"F1.imprint","IMPRINT",EDGE,{"derivedFrom":subQ3}),1.0]])]});}
            var Q4;
            {var subQ1=sQuery(id+"F0.wireOp",EDGE,"E98");Q4=makeQuery(id+"F0.imprint","IMPRINT",FACE,{"disambiguationData":[TD([[makeQuery(id+"F0.imprint","IMPRINT",EDGE,{"derivedFrom":subQ1}),1.0]])]});}
            extrude(context, id + "F2", {"entities" : qUnion([Q0, Q1, Q2, Q3, Q4]), "depth" : 5 * mm});
        }
    });
